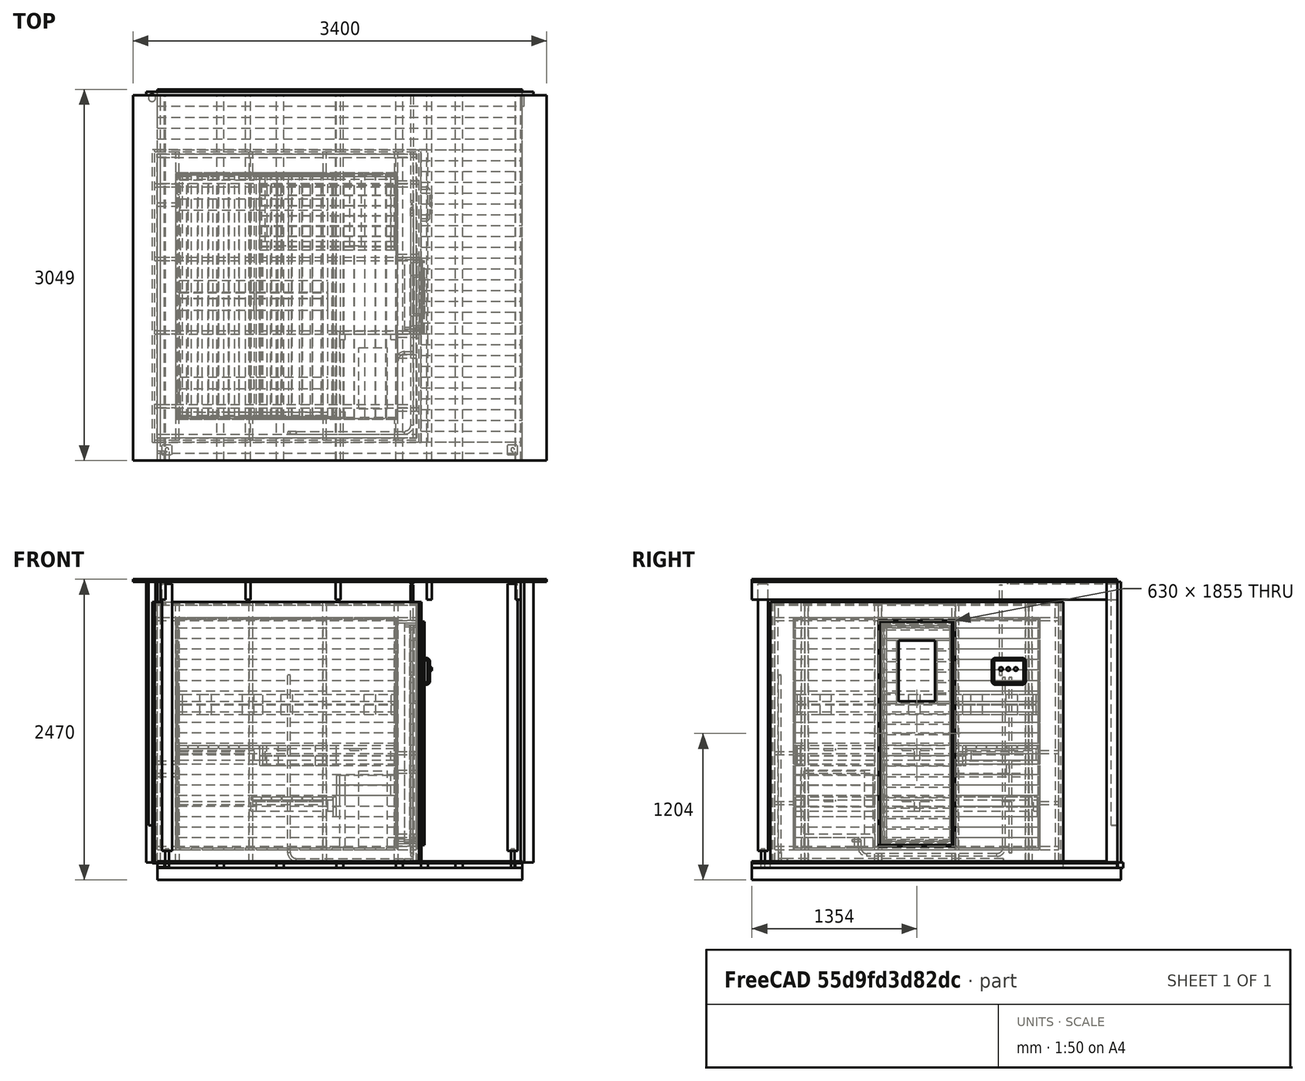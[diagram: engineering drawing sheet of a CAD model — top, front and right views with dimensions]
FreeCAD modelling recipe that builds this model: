
FCSTD DOCUMENT  (FreeCAD 0.18R16146 (Git))
Label: sauna v3
License: All rights reserved
LicenseURL: http://en.wikipedia.org/wiki/All_rights_reserved
objects: Part::Box×437, Part::Compound×38, Part::Cylinder×15, Part::Chamfer×7, Part::Torus×5, Part::Cut×5, Part::MultiFuse×4, App::DocumentObjectGroup×2, Part::Mirroring×2
note: 513 computed .brp shape members not serialized (recipe doc carries the construction recipe); baked Part::Feature solids carry a one-line shape summary decoded from their .brp

FEATURE [Part::Box] Box  label="Concrete base"
  AttacherType = Attacher::AttachEngine3D
  Height = 100
  Length = 3000
  Width = 3030
FEATURE [Part::Box] Box001  label="Wall"
  AttacherType = Attacher::AttachEngine3D
  Height = 2304
  Length = 3180
  Placement = pos=(-90,3003,144) rot=(0,0,1;0rad)
  Width = 27
FEATURE [Part::Box] Box001001  label="Wall001"
  AttacherType = Attacher::AttachEngine3D
  Height = 2304
  Length = 27
  Placement = pos=(0,2913,144) rot=(0,0,1;0rad)
  Width = 90
FEATURE [Part::Box] Box001001001  label="Wall002"
  AttacherType = Attacher::AttachEngine3D
  Height = 2304
  Length = 27
  Placement = pos=(2986,2913,144) rot=(0,0,1;0rad)
  Width = 90
FEATURE [Part::Box] Box001001002  label="Roof beam"
  AttacherType = Attacher::AttachEngine3D
  Height = 144
  Length = 3000
  Placement = pos=(69,0,2304) rot=(0,0,1;1.5708rad)
  Width = 42
FEATURE [Part::Cylinder] Cylinder  label="Pole base"
  Angle = 360
  AttacherType = Attacher::AttachEngine3D
  Height = 155
  Placement = pos=(80,90,100) rot=(0,0,1;0rad)
  Radius = 15
FEATURE [Part::Box] Box001001003  label="Pole"
  AttacherType = Attacher::AttachEngine3D
  Height = 2193
  Length = 82
  Placement = pos=(39,49,240) rot=(0,0,1;0rad)
  Width = 82
FEATURE [Part::Box] Box001001004  label="Pole support"
  AttacherType = Attacher::AttachEngine3D
  Height = 5
  Length = 100
  Placement = pos=(0,0,100) rot=(0,0,1;0rad)
  Width = 80
FEATURE [Part::Box] Box001001005  label="Roof"
  AttacherType = Attacher::AttachEngine3D
  Height = 22
  Length = 3400
  Placement = pos=(-200,0,2448) rot=(0,0,1;0rad)
  Width = 3000
FEATURE [Part::Cylinder] Cylinder001  label="Rainpipe"
  Angle = 360
  AttacherType = Attacher::AttachEngine3D
  Height = 2000
  Placement = pos=(-43,2980,448) rot=(0,0,1;0rad)
  Radius = 30
FEATURE [Part::Box] Box001001002001  label="Roof beam001"
  AttacherType = Attacher::AttachEngine3D
  Height = 144
  Length = 3000
  Placement = pos=(766,0,2304) rot=(0,0,1;1.5708rad)
  Width = 42
FEATURE [Part::Box] Box001001002001001  label="Roof beam002"
  AttacherType = Attacher::AttachEngine3D
  Height = 144
  Length = 3000
  Placement = pos=(1508,0,2304) rot=(0,0,1;1.5708rad)
  Width = 42
FEATURE [Part::Box] Box001001002001001001  label="Roof beam003"
  AttacherType = Attacher::AttachEngine3D
  Height = 144
  Length = 3000
  Placement = pos=(2255,0,2304) rot=(0,0,1;1.5708rad)
  Width = 42
FEATURE [Part::Box] Box001001002001001001001  label="Roof beam004"
  AttacherType = Attacher::AttachEngine3D
  Height = 144
  Length = 3000
  Placement = pos=(2986,0,2304) rot=(0,0,1;1.5708rad)
  Width = 42
FEATURE [Part::Cylinder] Cylinder002  label="Pole support001"
  Angle = 360
  AttacherType = Attacher::AttachEngine3D
  Height = 155
  Placement = pos=(2920,90,100) rot=(0,0,1;0rad)
  Radius = 15
FEATURE [Part::Box] Box001001003001  label="Pole001"
  AttacherType = Attacher::AttachEngine3D
  Height = 2193
  Length = 82
  Placement = pos=(2879,49,240) rot=(0,0,1;0rad)
  Width = 82
FEATURE [Part::Box] Box001001002001001001002  label="Wall base"
  AttacherType = Attacher::AttachEngine3D
  Height = 44
  Length = 3000
  Placement = pos=(0,3005,100) rot=(0,0,1;0rad)
  Width = 44
FEATURE [App::DocumentObjectGroup] Group  label="Available volume"
  Group = -> [Box,Box001,Box001001,Box001001001,Box001001002,Cylinder,Box001001003,Box001001004,Cylinder001,Box001001005,Box001001002001,Box001001002001001,Box001001002001001001,Box001001002001001001001,Cylinder002,Box001001003001,Box001001002001001001002]
FEATURE [Part::Box] Box001001002001001001003  label="B007"
  AttacherType = Attacher::AttachEngine3D
  Height = 100
  Length = 2075
  Placement = pos=(27.5,189,2158) rot=(0,0,1;0rad)
  Width = 27.5
FEATURE [Part::Box] Box001001002001001001003001  label="B008"
  AttacherType = Attacher::AttachEngine3D
  Height = 100
  Length = 2075
  Placement = pos=(27.5,434,2158) rot=(0,0,1;0rad)
  Width = 27.5
FEATURE [Part::Box] Box001001002001001001003002  label="A003"
  AttacherType = Attacher::AttachEngine3D
  Height = 100
  Length = 27.5
  Placement = pos=(0,189,2158) rot=(0,0,1;0rad)
  Width = 2330
FEATURE [Part::Box] Box001001002001001001003002001  label="A004"
  AttacherType = Attacher::AttachEngine3D
  Height = 100
  Length = 27.5
  Placement = pos=(2102.5,189,2158) rot=(0,0,1;0rad)
  Width = 2330
FEATURE [Part::Box] Box001001002001001001003002002  label="B009"
  AttacherType = Attacher::AttachEngine3D
  Height = 100
  Length = 2075
  Placement = pos=(27.5,1039,2158) rot=(0,0,1;0rad)
  Width = 27.5
FEATURE [Part::Box] Box001001002001001001003002003  label="B010"
  AttacherType = Attacher::AttachEngine3D
  Height = 100
  Length = 2075
  Placement = pos=(27.5,1644,2158) rot=(0,0,1;0rad)
  Width = 27.5
FEATURE [Part::Box] Box001001002001001001003002004  label="B011"
  AttacherType = Attacher::AttachEngine3D
  Height = 100
  Length = 2075
  Placement = pos=(27.5,2249,2158) rot=(0,0,1;0rad)
  Width = 27.5
FEATURE [Part::Box] Box001001002001001001003002005  label="B012"
  AttacherType = Attacher::AttachEngine3D
  Height = 100
  Length = 2075
  Placement = pos=(27.5,2491.5,2158) rot=(0,0,1;0rad)
  Width = 27.5
FEATURE [Part::Box] Box001001002001001001003002005003021  label="top OSB plate"
  AttacherType = Attacher::AttachEngine3D
  Height = 12
  Length = 2130
  Placement = pos=(0,189,2258) rot=(0,0,1;0rad)
  Width = 2330
FEATURE [Part::Box] Box001001002001001001003002005003022  label="I001"
  AttacherType = Attacher::AttachEngine3D
  Height = 26.5
  Length = 153
  Placement = pos=(0,189,250) rot=(0,0,1;0rad)
  Width = 2330
FEATURE [Part::Box] Box001001002001001001003002005003022001  label="I004"
  AttacherType = Attacher::AttachEngine3D
  Height = 26.5
  Length = 153
  Placement = pos=(1977,189,2131.5) rot=(0,0,1;0rad)
  Width = 2330
FEATURE [Part::Box] Box001001002001001001003002005003022001001  label="I003"
  AttacherType = Attacher::AttachEngine3D
  Height = 26.5
  Length = 153
  Placement = pos=(1977,189,250) rot=(0,0,1;0rad)
  Width = 2330
FEATURE [Part::Box] Box001001002001001001003002005003022001002  label="I002"
  AttacherType = Attacher::AttachEngine3D
  Height = 26.5
  Length = 153
  Placement = pos=(0,189,2131.5) rot=(0,0,1;0rad)
  Width = 2330
FEATURE [Part::Box] Box001001002001001001003002005003022001003  label="G001"
  AttacherType = Attacher::AttachEngine3D
  Height = 1855
  Length = 153
  Placement = pos=(0,189,276.5) rot=(0,0,1;0rad)
  Width = 26.5
FEATURE [Part::Box] Box001001002001001001003002005003022001003001  label="G002"
  AttacherType = Attacher::AttachEngine3D
  Height = 1855
  Length = 153
  Placement = pos=(0,436,276.5) rot=(0,0,1;0rad)
  Width = 26.5
FEATURE [Part::Box] Box001001002001001001003002005003022001003002  label="G003"
  AttacherType = Attacher::AttachEngine3D
  Height = 1855
  Length = 153
  Placement = pos=(0,1041,276.5) rot=(0,0,1;0rad)
  Width = 26.5
FEATURE [Part::Box] Box001001002001001001003002005003022001003003  label="G004"
  AttacherType = Attacher::AttachEngine3D
  Height = 1855
  Length = 153
  Placement = pos=(0,1646,276.5) rot=(0,0,1;0rad)
  Width = 26.5
FEATURE [Part::Box] Box001001002001001001003002005003022001003004  label="G005"
  AttacherType = Attacher::AttachEngine3D
  Height = 1855
  Length = 153
  Placement = pos=(0,2249,276.5) rot=(0,0,1;0rad)
  Width = 26.5
FEATURE [Part::Box] Box001001002001001001003002005003022001003004001  label="G006"
  AttacherType = Attacher::AttachEngine3D
  Height = 1855
  Length = 153
  Placement = pos=(0,2492.5,276.5) rot=(0,0,1;0rad)
  Width = 26.5
FEATURE [Part::Box] Box001001002001001001003002005003022001003004002001  label="F002"
  AttacherType = Attacher::AttachEngine3D
  Height = 26.5
  Length = 1824
  Placement = pos=(153,189,2131.5) rot=(0,0,1;0rad)
  Width = 153
FEATURE [Part::Box] Box001001002001001001003002005003022001003004002001001  label="F003"
  AttacherType = Attacher::AttachEngine3D
  Height = 26.5
  Length = 1824
  Placement = pos=(153,2366,2131.5) rot=(0,0,1;0rad)
  Width = 153
FEATURE [Part::Box] Box001001002001001001003002005003022001003004002001002  label="F004"
  AttacherType = Attacher::AttachEngine3D
  Height = 26.5
  Length = 1824
  Placement = pos=(153,2366,250) rot=(0,0,1;0rad)
  Width = 153
FEATURE [Part::Box] Box001001002001001001003002005003022001003001001  label="G007"
  AttacherType = Attacher::AttachEngine3D
  Height = 1855
  Length = 26.5
  Placement = pos=(153,2366,276.5) rot=(0,0,1;0rad)
  Width = 153
FEATURE [Part::Box] Box001001002001001001003002005003022001003001001001  label="G008"
  AttacherType = Attacher::AttachEngine3D
  Height = 1855
  Length = 26.5
  Placement = pos=(757.5,2366,276.5) rot=(0,0,1;0rad)
  Width = 153
FEATURE [Part::Box] Box001001002001001001003002005003022001003001001002  label="G009"
  AttacherType = Attacher::AttachEngine3D
  Height = 1855
  Length = 26.5
  Placement = pos=(1362,2366,276.5) rot=(0,0,1;0rad)
  Width = 153
FEATURE [Part::Box] Box001001002001001001003002005003022001003001001002001  label="G010"
  AttacherType = Attacher::AttachEngine3D
  Height = 1855
  Length = 26.5
  Placement = pos=(1950.5,2366,276.5) rot=(0,0,1;0rad)
  Width = 153
FEATURE [Part::Box] Box001001002001001001003002005003022001003004002001003  label="M001"
  AttacherType = Attacher::AttachEngine3D
  Height = 26.5
  Length = 578
  Placement = pos=(179.5,189,1029) rot=(0,0,1;0rad)
  Width = 153
FEATURE [Part::Box] Box001001002001001001003002005003022001003004002001003001  label="M002"
  AttacherType = Attacher::AttachEngine3D
  Height = 26.5
  Length = 578
  Placement = pos=(784,189,619) rot=(0,0,1;0rad)
  Width = 153
FEATURE [Part::Box] Box001001002001001001003002005003022001003001001002002  label="G011"
  AttacherType = Attacher::AttachEngine3D
  Height = 1855
  Length = 26.5
  Placement = pos=(153,189,276.5) rot=(0,0,1;0rad)
  Width = 153
FEATURE [Part::Box] Box001001002001001001003002005003022001003004002001003002  label="M003"
  AttacherType = Attacher::AttachEngine3D
  Height = 26.5
  Length = 578
  Placement = pos=(179.5,2366,1039) rot=(0,0,1;0rad)
  Width = 153
FEATURE [Part::Box] Box001001002001001001003002005003022001003004002001003001001  label="M004"
  AttacherType = Attacher::AttachEngine3D
  Height = 26.5
  Length = 578
  Placement = pos=(784,2366,619) rot=(0,0,1;0rad)
  Width = 153
FEATURE [Part::Box] Box001001002001001001003002005003022001003001001001001  label="G012"
  AttacherType = Attacher::AttachEngine3D
  Height = 1855
  Length = 26.5
  Placement = pos=(757.5,189,276.5) rot=(0,0,1;0rad)
  Width = 153
FEATURE [Part::Box] Box001001002001001001003002005003022001003001001002003  label="G013"
  AttacherType = Attacher::AttachEngine3D
  Height = 1855
  Length = 26.5
  Placement = pos=(1362,189,276.5) rot=(0,0,1;0rad)
  Width = 153
FEATURE [Part::Box] Box001001002001001001003002005003022001003001001002001001  label="G014"
  AttacherType = Attacher::AttachEngine3D
  Height = 1855
  Length = 26.5
  Placement = pos=(1950.5,189,276.5) rot=(0,0,1;0rad)
  Width = 153
FEATURE [Part::Box] Box001001002001001001003002005003022001003004002  label="F001"
  AttacherType = Attacher::AttachEngine3D
  Height = 26.5
  Length = 1824
  Placement = pos=(153,189,250) rot=(0,0,1;0rad)
  Width = 153
FEATURE [Part::Box] Box001001002001001001003002005003022001003004002001003001002  label="G015"
  AttacherType = Attacher::AttachEngine3D
  Height = 1855
  Length = 153
  Placement = pos=(1977,189,276.5) rot=(0,0,1;0rad)
  Width = 26.5
FEATURE [Part::Box] Box001001002001001001003002005003022001003001001002001002  label="G016"
  AttacherType = Attacher::AttachEngine3D
  Height = 1855
  Length = 153
  Placement = pos=(1977,408,276.5) rot=(0,0,1;0rad)
  Width = 26.5
FEATURE [Part::Box] Box001001002001001001003002005003022001003002001  label="G017"
  AttacherType = Attacher::AttachEngine3D
  Height = 1855
  Length = 153
  Placement = pos=(1977,1012.5,276.5) rot=(0,0,1;0rad)
  Width = 26.5
FEATURE [Part::Box] Box001001002001001001003002005003022001003003001  label="G018"
  AttacherType = Attacher::AttachEngine3D
  Height = 1855
  Length = 153
  Placement = pos=(1977,1669,276.5) rot=(0,0,1;0rad)
  Width = 26.5
FEATURE [Part::Box] Box001001002001001001003002005003022001003004002001003001003  label="G019"
  AttacherType = Attacher::AttachEngine3D
  Height = 1855
  Length = 153
  Placement = pos=(1977,2273.5,276.5) rot=(0,0,1;0rad)
  Width = 26.5
FEATURE [Part::Box] Box001001002001001001003002005003022001003004001001  label="G020"
  AttacherType = Attacher::AttachEngine3D
  Height = 1855
  Length = 153
  Placement = pos=(1977,2492.5,276.5) rot=(0,0,1;0rad)
  Width = 26.5
FEATURE [Part::Box] Box001001002001001001003002005003022001003004002001003001004  label="M005"
  AttacherType = Attacher::AttachEngine3D
  Height = 26.5
  Length = 153
  Placement = pos=(1977,434.5,877) rot=(0,0,1;0rad)
  Width = 578
FEATURE [Part::Box] Box001001002001001001003002005003022001003004002001003001004001  label="M006"
  AttacherType = Attacher::AttachEngine3D
  Height = 26.5
  Length = 153
  Placement = pos=(1977,1695.5,1029) rot=(0,0,1;0rad)
  Width = 578
FEATURE [Part::Box] Box001001002001001001003002005003022001003004002001003001004002  label="Y001"
  AttacherType = Attacher::AttachEngine3D
  Height = 95
  Length = 15
  Placement = pos=(168,357,985) rot=(0,0,1;0rad)
  Width = 1994
FEATURE [Part::Box] Box001001002001001001003002005003022001003004002001003001004002001  label="Y002"
  AttacherType = Attacher::AttachEngine3D
  Height = 80
  Length = 25
  Placement = pos=(843,362,941) rot=(0,0,1;0rad)
  Width = 1371
FEATURE [Part::Box] Box001001002001001001003002005003022001003004002001003001004002002  label="Z001"
  AttacherType = Attacher::AttachEngine3D
  Height = 95
  Length = 616
  Placement = pos=(183,357,985) rot=(0,0,1;0rad)
  Width = 44
FEATURE [Part::Box] Box001001002001001001003002005003022001003004002001003001004002002001  label="Z002"
  AttacherType = Attacher::AttachEngine3D
  Height = 95
  Length = 616
  Placement = pos=(183,2307,985) rot=(0,0,1;0rad)
  Width = 44
FEATURE [Part::Box] Box001001002001001001003002005003022001003004002001003001004002002001001  label="Z003"
  AttacherType = Attacher::AttachEngine3D
  Height = 95
  Length = 588
  Placement = pos=(814,2313,565) rot=(0,0,1;0rad)
  Width = 44
FEATURE [Part::Box] Box001001002001001001003002005003022001003004002001003001004002001001  label="J021"
  AttacherType = Attacher::AttachEngine3D
  Height = 80
  Length = 25
  Placement = pos=(1446,362,605) rot=(0,0,1;0rad)
  Width = 1984
FEATURE [Part::Box] Box001001002001001001003002005003022001003004002001003001004002002001002  label="Y004"
  AttacherType = Attacher::AttachEngine3D
  Height = 95
  Length = 44
  Placement = pos=(770,357,565) rot=(0,0,1;0rad)
  Width = 1994
FEATURE [Part::Box] Box001001002001001001003002005003022001003004002001003001004002002001003  label="Z004"
  AttacherType = Attacher::AttachEngine3D
  Height = 95
  Length = 588
  Placement = pos=(814,357,565) rot=(0,0,1;0rad)
  Width = 44
FEATURE [Part::Box] Box001001002001001001003002005003022001003004002001003001004002002001004  label="H001"
  AttacherType = Attacher::AttachEngine3D
  Height = 95
  Length = 1119
  Placement = pos=(843,2336,985) rot=(0,0,1;0rad)
  Width = 15
FEATURE [Part::Box] Box001001002001001001003002005003022001003004002001003001004002002001004001  label="H002"
  AttacherType = Attacher::AttachEngine3D
  Height = 80
  Length = 603
  Placement = pos=(868,372,1025) rot=(0,0,1;0rad)
  Width = 25
FEATURE [Part::Box] Box001001002001001001003002005003022001003004002001003001004002002001004002  label="AI001"
  AttacherType = Attacher::AttachEngine3D
  Height = 95
  Length = 44
  Placement = pos=(843,1802,985) rot=(0,0,1;0rad)
  Width = 534
FEATURE [Part::Box] Box001001002001001001003002005003022001003004002001003001004002002001004002001  label="AI002"
  AttacherType = Attacher::AttachEngine3D
  Height = 95
  Length = 44
  Placement = pos=(1918,1802,985) rot=(0,0,1;0rad)
  Width = 534
FEATURE [Part::Box] Box001001002001001001003002005003022001003004002001003001004002002001004002002  label="Z007"
  AttacherType = Attacher::AttachEngine3D
  Height = 95
  Length = 616
  Placement = pos=(183,1335,985) rot=(0,0,1;0rad)
  Width = 44
FEATURE [Part::Box] Box001001002001001001003002005003022001003004002001003001004002002001003001  label="Z008"
  AttacherType = Attacher::AttachEngine3D
  Height = 95
  Length = 588
  Placement = pos=(814,1335,565) rot=(0,0,1;0rad)
  Width = 44
FEATURE [Part::Box] Box001001002001001001003002005003022001003004002001003001004002002001004002003  label="J001"
  AttacherType = Attacher::AttachEngine3D
  Height = 25
  Length = 80
  Placement = pos=(171,362,1080) rot=(0,0,1;0rad)
  Width = 1984
FEATURE [Part::Box] Box001001002001001001003002005003022001003004002001003001004002002001004002003001  label="J002"
  AttacherType = Attacher::AttachEngine3D
  Height = 25
  Length = 80
  Placement = pos=(255,362,1080) rot=(0,0,1;0rad)
  Width = 1984
FEATURE [Part::Box] Box001001002001001001003002005003022001003004002001003001004002002001004002003002  label="J003"
  AttacherType = Attacher::AttachEngine3D
  Height = 25
  Length = 80
  Placement = pos=(339,362,1080) rot=(0,0,1;0rad)
  Width = 1984
FEATURE [Part::Box] Box001001002001001001003002005003022001003004002001003001004002002001004002003003  label="J004"
  AttacherType = Attacher::AttachEngine3D
  Height = 25
  Length = 80
  Placement = pos=(423,362,1080) rot=(0,0,1;0rad)
  Width = 1984
FEATURE [Part::Box] Box001001002001001001003002005003022001003004002001003001004002002001004002003004  label="J005"
  AttacherType = Attacher::AttachEngine3D
  Height = 25
  Length = 80
  Placement = pos=(507,362,1080) rot=(0,0,1;0rad)
  Width = 1984
FEATURE [Part::Box] Box001001002001001001003002005003022001003004002001003001004002002001004002003005  label="J006"
  AttacherType = Attacher::AttachEngine3D
  Height = 25
  Length = 80
  Placement = pos=(591,362,1080) rot=(0,0,1;0rad)
  Width = 1984
FEATURE [Part::Box] Box001001002001001001003002005003022001003004002001003001004002002001004002003005001  label="J007"
  AttacherType = Attacher::AttachEngine3D
  Height = 25
  Length = 80
  Placement = pos=(1278,362,660) rot=(0,0,1;0rad)
  Width = 1984
FEATURE [Part::Box] Box001001002001001001003002005003022001003004002001003001004002002001004002003005002  label="J008"
  AttacherType = Attacher::AttachEngine3D
  Height = 25
  Length = 80
  Placement = pos=(858,362,660) rot=(0,0,1;0rad)
  Width = 1984
FEATURE [Part::Box] Box001001002001001001003002005003022001003004002001003001004002002001004002003001001  label="J009"
  AttacherType = Attacher::AttachEngine3D
  Height = 25
  Length = 80
  Placement = pos=(942,362,660) rot=(0,0,1;0rad)
  Width = 1984
FEATURE [Part::Box] Box001001002001001001003002005003022001003004002001003001004002002001004002003002001  label="J010"
  AttacherType = Attacher::AttachEngine3D
  Height = 25
  Length = 80
  Placement = pos=(1026,362,660) rot=(0,0,1;0rad)
  Width = 1984
FEATURE [Part::Box] Box001001002001001001003002005003022001003004002001003001004002002001004002003003001  label="J011"
  AttacherType = Attacher::AttachEngine3D
  Height = 25
  Length = 80
  Placement = pos=(1110,362,660) rot=(0,0,1;0rad)
  Width = 1984
FEATURE [Part::Box] Box001001002001001001003002005003022001003004002001003001004002002001004002003004001  label="J012"
  AttacherType = Attacher::AttachEngine3D
  Height = 25
  Length = 80
  Placement = pos=(1194,362,660) rot=(0,0,1;0rad)
  Width = 1984
FEATURE [Part::Box] Box001001002001001001003002005003022001003004002001003001004002002001004002003005003  label="C001"
  AttacherType = Attacher::AttachEngine3D
  Height = 25
  Length = 1114
  Placement = pos=(843,1846,1080) rot=(0,0,1;0rad)
  Width = 80
FEATURE [Part::Box] Box001001002001001001003002005003022001003004002001003001004002002001004002003005003001  label="C002"
  AttacherType = Attacher::AttachEngine3D
  Height = 25
  Length = 1114
  Placement = pos=(843,1930,1080) rot=(0,0,1;0rad)
  Width = 80
FEATURE [Part::Box] Box001001002001001001003002005003022001003004002001003001004002002001004002003005003002  label="C003"
  AttacherType = Attacher::AttachEngine3D
  Height = 25
  Length = 1114
  Placement = pos=(843,2014,1080) rot=(0,0,1;0rad)
  Width = 80
FEATURE [Part::Box] Box001001002001001001003002005003022001003004002001003001004002002001004002003005003003  label="C004"
  AttacherType = Attacher::AttachEngine3D
  Height = 25
  Length = 1114
  Placement = pos=(843,2098,1080) rot=(0,0,1;0rad)
  Width = 80
FEATURE [Part::Box] Box001001002001001001003002005003022001003004002001003001004002002001004002003005003004  label="C005"
  AttacherType = Attacher::AttachEngine3D
  Height = 25
  Length = 1114
  Placement = pos=(843,2182,1080) rot=(0,0,1;0rad)
  Width = 80
FEATURE [Part::Box] Box001001002001001001003002005003022001003004002001003001004002002001004002003005003005  label="C006"
  AttacherType = Attacher::AttachEngine3D
  Height = 25
  Length = 1114
  Placement = pos=(843,2266,1080) rot=(0,0,1;0rad)
  Width = 80
FEATURE [Part::Box] Box001001002001001001003002005003022001003004002001003001004002002001004002003005003005001  label="D001"
  AttacherType = Attacher::AttachEngine3D
  Height = 15
  Length = 610
  Placement = pos=(186,2057,1065) rot=(0,0,1;0rad)
  Width = 95
FEATURE [Part::Box] Box001001002001001001003002005003022001003004002001003001004002002001004002003005003005001001  label="D002"
  AttacherType = Attacher::AttachEngine3D
  Height = 15
  Length = 610
  Placement = pos=(186,592,1065) rot=(0,0,1;0rad)
  Width = 95
FEATURE [Part::Box] Box001001002001001001003002005003022001003004002001003001004002002001004002003005003005001002  label="D003"
  AttacherType = Attacher::AttachEngine3D
  Height = 15
  Length = 586
  Placement = pos=(815,2057,645) rot=(0,0,1;0rad)
  Width = 95
FEATURE [Part::Box] Box001001002001001001003002005003022001003004002001003001004002002001004002003005003005001001001  label="D004"
  AttacherType = Attacher::AttachEngine3D
  Height = 15
  Length = 586
  Placement = pos=(815,592,645) rot=(0,0,1;0rad)
  Width = 95
FEATURE [Part::Box] Box001001002001001001003002005003022001003004002001003001004002002001004002003005003005001001002  label="D005"
  AttacherType = Attacher::AttachEngine3D
  Height = 15
  Length = 95
  Placement = pos=(984,1767,1065) rot=(0,0,1;0rad)
  Width = 568
FEATURE [Part::Box] Box001001002001001001003002005003022001003004002001003001004002002001004002003005003005001001002001  label="D006"
  AttacherType = Attacher::AttachEngine3D
  Height = 15
  Length = 95
  Placement = pos=(1584,1767,1065) rot=(0,0,1;0rad)
  Width = 568
FEATURE [Part::Box] Box001001002001001001003002005003022001003004002001003001004002002001004002003005003005001001002002  label="M007"
  AttacherType = Attacher::AttachEngine3D
  Height = 26.5
  Length = 578
  Placement = pos=(179.5,189,619) rot=(0,0,1;0rad)
  Width = 153
FEATURE [Part::Box] Box001001002001001001003002005003022001003004002001003001001001  label="M008"
  AttacherType = Attacher::AttachEngine3D
  Height = 26.5
  Length = 578
  Placement = pos=(179.5,2366,619) rot=(0,0,1;0rad)
  Width = 153
FEATURE [Part::Box] Box001001002001001001003002005003022001003004002001003001004002002001004002003005003005001001002003  label="J013"
  AttacherType = Attacher::AttachEngine3D
  Height = 25
  Length = 80
  Placement = pos=(675,362,1080) rot=(0,0,1;0rad)
  Width = 1984
FEATURE [Part::Box] Box001001002001001001003002005003022001003004002001003001004002002001004002003005001001  label="J014"
  AttacherType = Attacher::AttachEngine3D
  Height = 25
  Length = 80
  Placement = pos=(1362,362,660) rot=(0,0,1;0rad)
  Width = 1984
FEATURE [Part::Box] Box001001002001001001003002005003022001003004002001003001004002002001004002003005003005001001002004  label="Heather"
  AttacherType = Attacher::AttachEngine3D
  Height = 630
  Length = 235
  Placement = pos=(1657,427,265) rot=(0,0,1;0rad)
  Width = 500
FEATURE [Part::Box] Box001001002001001001003002005003022001003004002001003001004002002001004002003005001001001001  label="AA001"
  AttacherType = Attacher::AttachEngine3D
  Height = 80
  Length = 25
  Placement = pos=(1475,357,698) rot=(0,0,1;0rad)
  Width = 707
FEATURE [Part::Box] Box001001002001001001003002005003022001003004002001003001004002002001004002003005001001001001001  label="AA002"
  AttacherType = Attacher::AttachEngine3D
  Height = 80
  Length = 25
  Placement = pos=(1475,357,782) rot=(0,0,1;0rad)
  Width = 707
FEATURE [Part::Box] Box001001002001001001003002005003022001003004002001003001004002002001004002003005001001001001001001  label="AB001"
  AttacherType = Attacher::AttachEngine3D
  Height = 80
  Length = 472
  Placement = pos=(1500,1039,782) rot=(0,0,1;0rad)
  Width = 25
FEATURE [Part::Box] Box001001002001001001003002005003022001003004002001003001004002002001004002003005001001001001001001001  label="AB002"
  AttacherType = Attacher::AttachEngine3D
  Height = 80
  Length = 472
  Placement = pos=(1500,1039,698) rot=(0,0,1;0rad)
  Width = 25
FEATURE [Part::Box] Box001001002001001001003002005003022001003004002001003001004002002001004002003005001001001001001001002  label="AC001"
  AttacherType = Attacher::AttachEngine3D
  Height = 592
  Length = 44
  Placement = pos=(1500,995,270) rot=(0,0,1;0rad)
  Width = 44
FEATURE [Part::Box] Box001001002001001001003002005003022001003004002001003001004002002001004002003005001001001001001001002001  label="AD001"
  AttacherType = Attacher::AttachEngine3D
  Height = 164
  Length = 44
  Placement = pos=(1500,357,698) rot=(0,0,1;0rad)
  Width = 44
FEATURE [Part::Box] Box001001002001001001003002005003022001003004002001003001004002002001004002003005001001001001001001002001001  label="AD002"
  AttacherType = Attacher::AttachEngine3D
  Height = 164
  Length = 44
  Placement = pos=(1918,995,698) rot=(0,0,1;0rad)
  Width = 44
FEATURE [Part::Box] Box001001002001001001003002005003022001003004002001003001004002002001004002003005003005001001002005  label="D007"
  AttacherType = Attacher::AttachEngine3D
  Height = 15
  Length = 610
  Placement = pos=(186,1235,1065) rot=(0,0,1;0rad)
  Width = 95
FEATURE [Part::Box] Box001001002001001001003002005003022001003004002001003001004002002001004002003005003005001001002006  label="D008"
  AttacherType = Attacher::AttachEngine3D
  Height = 15
  Length = 610
  Placement = pos=(186,1385,1065) rot=(0,0,1;0rad)
  Width = 95
FEATURE [Part::Box] Box001001002001001001003002005003022001003004002001003001004002002001004002003005003005001002001  label="D009"
  AttacherType = Attacher::AttachEngine3D
  Height = 15
  Length = 586
  Placement = pos=(815,1385,645) rot=(0,0,1;0rad)
  Width = 95
FEATURE [Part::Box] Box001001002001001001003002005003022001003004002001003001004002002001004002003005003005001002002  label="D010"
  AttacherType = Attacher::AttachEngine3D
  Height = 15
  Length = 586
  Placement = pos=(815,1235,645) rot=(0,0,1;0rad)
  Width = 95
FEATURE [Part::Box] Box001001002001001001003002005003022001003004002001003001004002002001004002003005001001001001001001002001002  label="J015"
  AttacherType = Attacher::AttachEngine3D
  Height = 80
  Length = 25
  Placement = pos=(1922,1733,1361) rot=(0,0,1;0rad)
  Width = 578
FEATURE [Part::Box] Box001001002001001001003002005003022001003004002001003001004002002001004002003005001001001001001001002001002001  label="J016"
  AttacherType = Attacher::AttachEngine3D
  Height = 80
  Length = 25
  Placement = pos=(183,372,1445) rot=(0,0,1;0rad)
  Width = 1964
FEATURE [Part::Box] Box001001002001001001003002005003022001003004002001003001004002002001004002003005001001001001001001002001002001001  label="AE001"
  AttacherType = Attacher::AttachEngine3D
  Height = 164
  Length = 15
  Placement = pos=(168,559,1361) rot=(0,0,1;0rad)
  Width = 95
FEATURE [Part::Box] Box001001002001001001003002005003022001003004002001003001004002002001004002003005001001001001001001002001002001001001  label="AE002"
  AttacherType = Attacher::AttachEngine3D
  Height = 164
  Length = 15
  Placement = pos=(168,1289,1361) rot=(0,0,1;0rad)
  Width = 95
FEATURE [Part::Box] Box001001002001001001003002005003022001003004002001003001004002002001004002003005001001001001001001002001002001001002  label="AE003"
  AttacherType = Attacher::AttachEngine3D
  Height = 164
  Length = 15
  Placement = pos=(168,2089,1361) rot=(0,0,1;0rad)
  Width = 95
FEATURE [Part::Box] Box001001002001001001003002005003022001003004002001003001004002002001004002003005001001001001001001002001002001001003  label="AF001"
  AttacherType = Attacher::AttachEngine3D
  Height = 80
  Length = 660
  Placement = pos=(207,372,1361) rot=(0,0,1;0rad)
  Width = 25
FEATURE [Part::Box] Box001001002001001001003002005003022001003004002001003001004002002001004002003005001001001001001001002001002001001004  label="M009"
  AttacherType = Attacher::AttachEngine3D
  Height = 26.5
  Length = 153
  Placement = pos=(1977,434.5,352) rot=(0,0,1;0rad)
  Width = 578
FEATURE [Part::Box] Box001001002001001001003002005003022001003001001002001002001  label="AH002"
  AttacherType = Attacher::AttachEngine3D
  Height = 75
  Length = 153
  Placement = pos=(1977,844,277) rot=(0,0,1;0rad)
  Width = 26.5
FEATURE [Part::Box] Box001001002001001001003002005003022001003004002001003001004002002001004002003005001001001001001001002001002001001003001  label="AF002"
  AttacherType = Attacher::AttachEngine3D
  Height = 80
  Length = 1739
  Placement = pos=(208,2311,1445) rot=(0,0,1;0rad)
  Width = 25
FEATURE [Part::Box] Box001001002001001001003002005003022001003004002001003001004002002001004002003005001001001001001001002001002001001003002  label="AE004"
  AttacherType = Attacher::AttachEngine3D
  Height = 164
  Length = 95
  Placement = pos=(350,2336,1361) rot=(0,0,1;0rad)
  Width = 15
FEATURE [Part::Box] Box001001002001001001003002005003022001003004002001003001004002002001004002003005001001001001001001002001002001001003002001  label="AE005"
  AttacherType = Attacher::AttachEngine3D
  Height = 164
  Length = 95
  Placement = pos=(1016,2336,1361) rot=(0,0,1;0rad)
  Width = 15
FEATURE [Part::Box] Box001001002001001001003002005003022001003004002001003001004002002001004002003005001001001001001001002001002001001003002002  label="AE006"
  AttacherType = Attacher::AttachEngine3D
  Height = 164
  Length = 95
  Placement = pos=(1700,2336,1361) rot=(0,0,1;0rad)
  Width = 15
FEATURE [Part::Box] Box001001002001001001003002005003022001003004002001003001004002002001004002003005001001001001001001002001002001001004001  label="M010"
  AttacherType = Attacher::AttachEngine3D
  Height = 26.5
  Length = 153
  Placement = pos=(0,1671,951.5) rot=(0,0,1;0rad)
  Width = 578
FEATURE [Part::Box] Box001001002001001001003002005003022001003004002001003001004002002001004002003005001001001001001001002001002001001004001001  label="M011"
  AttacherType = Attacher::AttachEngine3D
  Height = 26.5
  Length = 153
  Placement = pos=(0,1671,850) rot=(0,0,1;0rad)
  Width = 578
FEATURE [Part::Box] Box001001002001001001003002005003022001003004002001003001004002002001004002003005001001001001001001002001002001001004001001001  label="AH001"
  AttacherType = Attacher::AttachEngine3D
  Height = 75
  Length = 153
  Placement = pos=(0,2091,876.5) rot=(0,0,1;0rad)
  Width = 26.5
FEATURE [Part::Box] Box001001002001001001003002005003022001003004002001003001004002002001004002003005001001001001001001002001002001001004001001002  label="Terrasbalk001"
  AttacherType = Attacher::AttachEngine3D
  Height = 38
  Length = 58
  Placement = pos=(0,0,100) rot=(0,0,1;0rad)
  Width = 3000
FEATURE [Part::Box] Box001001002001001001003002005003022001003004002001003001004002002001004002003005001001001001001001002001002001001004001001002001  label="Terrasbalk002"
  AttacherType = Attacher::AttachEngine3D
  Height = 38
  Length = 58
  Placement = pos=(490,0,100) rot=(0,0,1;0rad)
  Width = 3000
FEATURE [Part::Box] Box001001002001001001003002005003022001003004002001003001004002002001004002003005001001001001001001002001002001001004001001002002  label="Terrasbalk003"
  AttacherType = Attacher::AttachEngine3D
  Height = 38
  Length = 58
  Placement = pos=(980,0,100) rot=(0,0,1;0rad)
  Width = 3000
FEATURE [Part::Box] Box001001002001001001003002005003022001003004002001003001004002002001004002003005001001001001001001002001002001001004001001002002001005005  label="Terrasplank001"
  AttacherType = Attacher::AttachEngine3D
  Height = 15.5
  Length = 3000
  Placement = pos=(0,0,138) rot=(0,0,1;0rad)
  Width = 63
FEATURE [Part::Box] Box001001002001001001003002005003022001003004002001003001004002002001004002003005001001001001001001002001002001001004001001002002001005005001  label="Terrasplank002"
  AttacherType = Attacher::AttachEngine3D
  Height = 15.5
  Length = 3000
  Placement = pos=(0,63,138) rot=(0,0,1;0rad)
  Width = 89
FEATURE [Part::Box] Box001001002001001001003002005003022001003004002001003001004002002001004002003005001001001001001001002001002001001004001001002002001005005002  label="TerrasplankA001"
  AttacherType = Attacher::AttachEngine3D
  Height = 15.5
  Length = 833
  Placement = pos=(2167,152,138) rot=(0,0,1;0rad)
  Width = 89
FEATURE [Part::Box] Box001001002001001001003002005003022001003004002001003001004002002001004002003005001001001001001001002001002001001004001001002002001005005002001  label="TerrasplankA002"
  AttacherType = Attacher::AttachEngine3D
  Height = 15.5
  Length = 833
  Placement = pos=(2167,241,138) rot=(0,0,1;0rad)
  Width = 89
FEATURE [Part::Box] Box001001002001001001003002005003022001003004002001003001004002002001004002003005001001001001001001002001002001001004001001002002001005005002002  label="TerrasplankA003"
  AttacherType = Attacher::AttachEngine3D
  Height = 15.5
  Length = 833
  Placement = pos=(2167,330,138) rot=(0,0,1;0rad)
  Width = 89
FEATURE [Part::Box] Box001001002001001001003002005003022001003004002001003001004002002001004002003005001001001001001001002001002001001004001001002002001005005002003  label="TerrasplankA004"
  AttacherType = Attacher::AttachEngine3D
  Height = 15.5
  Length = 833
  Placement = pos=(2167,419,138) rot=(0,0,1;0rad)
  Width = 89
FEATURE [Part::Box] Box001001002001001001003002005003022001003004002001003001004002002001004002003005001001001001001001002001002001001004001001002002001005005002004  label="TerrasplankA005"
  AttacherType = Attacher::AttachEngine3D
  Height = 15.5
  Length = 833
  Placement = pos=(2167,508,138) rot=(0,0,1;0rad)
  Width = 89
FEATURE [Part::Box] Box001001002001001001003002005003022001003004002001003001004002002001004002003005001001001001001001002001002001001004001001002002001005005002005  label="TerrasplankA006"
  AttacherType = Attacher::AttachEngine3D
  Height = 15.5
  Length = 833
  Placement = pos=(2167,597,138) rot=(0,0,1;0rad)
  Width = 89
FEATURE [Part::Box] Box001001002001001001003002005003022001003004002001003001004002002001004002003005001001001001001001002001002001001004001001002002001005005002006  label="TerrasplankA007"
  AttacherType = Attacher::AttachEngine3D
  Height = 15.5
  Length = 833
  Placement = pos=(2167,686,138) rot=(0,0,1;0rad)
  Width = 89
FEATURE [Part::Box] Box001001002001001001003002005003022001003004002001003001004002002001004002003005001001001001001001002001002001001004001001002002001005005002007  label="TerrasplankA008"
  AttacherType = Attacher::AttachEngine3D
  Height = 15.5
  Length = 833
  Placement = pos=(2167,775,138) rot=(0,0,1;0rad)
  Width = 89
FEATURE [Part::Box] Box001001002001001001003002005003022001003004002001003001004002002001004002003005001001001001001001002001002001001004001001002002001005005002008  label="TerrasplankA009"
  AttacherType = Attacher::AttachEngine3D
  Height = 15.5
  Length = 833
  Placement = pos=(2167,864,138) rot=(0,0,1;0rad)
  Width = 89
FEATURE [Part::Box] Box001001002001001001003002005003022001003004002001003001004002002001004002003005001001001001001001002001002001001004001001002002001005005002009  label="TerrasplankA010"
  AttacherType = Attacher::AttachEngine3D
  Height = 15.5
  Length = 833
  Placement = pos=(2167,953,138) rot=(0,0,1;0rad)
  Width = 89
FEATURE [Part::Box] Box001001002001001001003002005003022001003004002001003001004002002001004002003005001001001001001001002001002001001004001001002002001005005002010  label="TerrasplankA011"
  AttacherType = Attacher::AttachEngine3D
  Height = 15.5
  Length = 833
  Placement = pos=(2167,1042,138) rot=(0,0,1;0rad)
  Width = 89
FEATURE [Part::Box] Box001001002001001001003002005003022001003004002001003001004002002001004002003005001001001001001001002001002001001004001001002002001005005002010001  label="TerrasplankA012"
  AttacherType = Attacher::AttachEngine3D
  Height = 15.5
  Length = 833
  Placement = pos=(2167,1131,138) rot=(0,0,1;0rad)
  Width = 89
FEATURE [Part::Box] Box001001002001001001003002005003022001003004002001003001004002002001004002003005001001001001001001002001002001001004001001002002001005005002010002  label="TerrasplankA013"
  AttacherType = Attacher::AttachEngine3D
  Height = 15.5
  Length = 833
  Placement = pos=(2167,1220,138) rot=(0,0,1;0rad)
  Width = 89
FEATURE [Part::Box] Box001001002001001001003002005003022001003004002001003001004002002001004002003005001001001001001001002001002001001004001001002002001005005002010003  label="TerrasplankA014"
  AttacherType = Attacher::AttachEngine3D
  Height = 15.5
  Length = 833
  Placement = pos=(2167,1309,138) rot=(0,0,1;0rad)
  Width = 89
FEATURE [Part::Box] Box001001002001001001003002005003022001003004002001003001004002002001004002003005001001001001001001002001002001001004001001002002001005005002010004  label="TerrasplankA015"
  AttacherType = Attacher::AttachEngine3D
  Height = 15.5
  Length = 833
  Placement = pos=(2167,1398,138) rot=(0,0,1;0rad)
  Width = 89
FEATURE [Part::Box] Box001001002001001001003002005003022001003004002001003001004002002001004002003005001001001001001001002001002001001004001001002002001005005002010005  label="TerrasplankA016"
  AttacherType = Attacher::AttachEngine3D
  Height = 15.5
  Length = 833
  Placement = pos=(2167,1487,138) rot=(0,0,1;0rad)
  Width = 89
FEATURE [Part::Box] Box001001002001001001003002005003022001003004002001003001004002002001004002003005001001001001001001002001002001001004001001002002001005005002010006  label="TerrasplankA017"
  AttacherType = Attacher::AttachEngine3D
  Height = 15.5
  Length = 833
  Placement = pos=(2167,1576,138) rot=(0,0,1;0rad)
  Width = 89
FEATURE [Part::Box] Box001001002001001001003002005003022001003004002001003001004002002001004002003005001001001001001001002001002001001004001001002002001005005002010007  label="TerrasplankA018"
  AttacherType = Attacher::AttachEngine3D
  Height = 15.5
  Length = 833
  Placement = pos=(2167,1665,138) rot=(0,0,1;0rad)
  Width = 89
FEATURE [Part::Box] Box001001002001001001003002005003022001003004002001003001004002002001004002003005001001001001001001002001002001001004001001002002001005005002010008  label="TerrasplankA019"
  AttacherType = Attacher::AttachEngine3D
  Height = 15.5
  Length = 833
  Placement = pos=(2167,1754,138) rot=(0,0,1;0rad)
  Width = 89
FEATURE [Part::Box] Box001001002001001001003002005003022001003004002001003001004002002001004002003005001001001001001001002001002001001004001001002002001005005002010009  label="TerrasplankA020"
  AttacherType = Attacher::AttachEngine3D
  Height = 15.5
  Length = 833
  Placement = pos=(2167,1843,138) rot=(0,0,1;0rad)
  Width = 89
FEATURE [Part::Box] Box001001002001001001003002005003022001003004002001003001004002002001004002003005001001001001001001002001002001001004001001002002001005005002010010  label="TerrasplankA021"
  AttacherType = Attacher::AttachEngine3D
  Height = 15.5
  Length = 833
  Placement = pos=(2167,1932,138) rot=(0,0,1;0rad)
  Width = 89
FEATURE [Part::Box] Box001001002001001001003002005003022001003004002001003001004002002001004002003005001001001001001001002001002001001004001001002002001005005002010011  label="TerrasplankA022"
  AttacherType = Attacher::AttachEngine3D
  Height = 15.5
  Length = 833
  Placement = pos=(2167,2021,138) rot=(0,0,1;0rad)
  Width = 89
FEATURE [Part::Box] Box001001002001001001003002005003022001003004002001003001004002002001004002003005001001001001001001002001002001001004001001002002001005005002010012  label="TerrasplankA023"
  AttacherType = Attacher::AttachEngine3D
  Height = 15.5
  Length = 833
  Placement = pos=(2167,2110,138) rot=(0,0,1;0rad)
  Width = 89
FEATURE [Part::Box] Box001001002001001001003002005003022001003004002001003001004002002001004002003005001001001001001001002001002001001004001001002002001005005002010013  label="TerrasplankA024"
  AttacherType = Attacher::AttachEngine3D
  Height = 15.5
  Length = 833
  Placement = pos=(2167,2199,138) rot=(0,0,1;0rad)
  Width = 89
FEATURE [Part::Box] Box001001002001001001003002005003022001003004002001003001004002002001004002003005001001001001001001002001002001001004001001002002001005005002010014  label="TerrasplankA025"
  AttacherType = Attacher::AttachEngine3D
  Height = 15.5
  Length = 833
  Placement = pos=(2167,2288,138) rot=(0,0,1;0rad)
  Width = 89
FEATURE [Part::Box] Box001001002001001001003002005003022001003004002001003001004002002001004002003005001001001001001001002001002001001004001001002002001005005002010015  label="TerrasplankA026"
  AttacherType = Attacher::AttachEngine3D
  Height = 15.5
  Length = 833
  Placement = pos=(2167,2377,138) rot=(0,0,1;0rad)
  Width = 89
FEATURE [Part::Box] Box001001002001001001003002005003022001003004002001003001004002002001004002003005001001001001001001002001002001001004001001002002001005005002010015001  label="TerrasplankA027"
  AttacherType = Attacher::AttachEngine3D
  Height = 15.5
  Length = 833
  Placement = pos=(2167,2466,138) rot=(0,0,1;0rad)
  Width = 89
FEATURE [Part::Box] Box001001002001001001003002005003022001003004002001003001004002002001004002003005001001001001001001002001002001001004001001002002001005005002010015002  label="Terrasplank003"
  AttacherType = Attacher::AttachEngine3D
  Height = 15.5
  Length = 3000
  Placement = pos=(0,2555,138) rot=(0,0,1;0rad)
  Width = 89
FEATURE [Part::Box] Box001001002001001001003002005003022001003004002001003001004002002001004002003005001001001001001001002001002001001004001001002002001005005002010015002001  label="Terrasplank004"
  AttacherType = Attacher::AttachEngine3D
  Height = 15.5
  Length = 3000
  Placement = pos=(0,2644,138) rot=(0,0,1;0rad)
  Width = 89
FEATURE [Part::Box] Box001001002001001001003002005003022001003004002001003001004002002001004002003005001001001001001001002001002001001004001001002002001005005002010015002002  label="Terrasplank005"
  AttacherType = Attacher::AttachEngine3D
  Height = 15.5
  Length = 3000
  Placement = pos=(0,2733,138) rot=(0,0,1;0rad)
  Width = 89
FEATURE [Part::Box] Box001001002001001001003002005003022001003004002001003001004002002001004002003005001001001001001001002001002001001004001001002002001005005002010015002003  label="Terrasplank006"
  AttacherType = Attacher::AttachEngine3D
  Height = 15.5
  Length = 3000
  Placement = pos=(0,2822,138) rot=(0,0,1;0rad)
  Width = 89
FEATURE [Part::Box] Box001001002001001001003002005003022001003004002001003001004002002001004002003005001001001001001001002001002001001004001001002002001005005002010015002004  label="Terrasplank007"
  AttacherType = Attacher::AttachEngine3D
  Height = 15.5
  Length = 3000
  Placement = pos=(0,2911,138) rot=(0,0,1;0rad)
  Width = 89
FEATURE [Part::Torus] Torus001001  label="230Vlicht002"
  Angle1 = -180
  Angle2 = 180
  Angle3 = 90
  AttacherType = Attacher::AttachEngine3D
  Placement = pos=(2091,2065,225) rot=(0,1,0;1.5708rad)
  Radius1 = 60
  Radius2 = 11
FEATURE [Part::Torus] Torus001002  label="230Vlight004"
  Angle1 = -180
  Angle2 = 180
  Angle3 = 90
  AttacherType = Attacher::AttachEngine3D
  Placement = pos=(2031,289,165) rot=(0,0,-1;1.5708rad)
  Radius1 = 60
  Radius2 = 11
FEATURE [Part::Mirroring] Part__Mirroring  label="230Vlight006"
  Base = (2000,2000,50)
  Normal = (0,1,0)
  Placement = pos=(-793,2320,1) rot=(0,0,-1;1.5708rad)
  Source = -> Torus001001
FEATURE [Part::Cylinder] Cylinder004  label="230Vlight003"
  Angle = 360
  AttacherType = Attacher::AttachEngine3D
  Height = 1776
  Placement = pos=(2091,2065,165) rot=(1,0,0;1.5708rad)
  Radius = 11
FEATURE [Part::Cylinder] Cylinder005  label="380Vin003"
  Angle = 360
  AttacherType = Attacher::AttachEngine3D
  Height = 745
  Placement = pos=(2091,2045,1680) rot=(0,0,1;0rad)
  Radius = 11
FEATURE [Part::Cylinder] Cylinder005001  label="230Vlight001"
  Angle = 360
  AttacherType = Attacher::AttachEngine3D
  Height = 1440
  Placement = pos=(2091,2125,225) rot=(0,0,1;0rad)
  Radius = 11
FEATURE [Part::Cylinder] Cylinder004001  label="380Vheater003"
  Angle = 360
  AttacherType = Attacher::AttachEngine3D
  Height = 1065
  Placement = pos=(2091,2010,205) rot=(1,0,0;1.5708rad)
  Radius = 11
FEATURE [Part::Torus] Torus001001001  label="380Vheater002"
  Angle1 = -180
  Angle2 = 180
  Angle3 = 90
  AttacherType = Attacher::AttachEngine3D
  Placement = pos=(2091,2010,265) rot=(0,1,0;1.5708rad)
  Radius1 = 60
  Radius2 = 11
FEATURE [Part::Cylinder] Cylinder005001001  label="380Vheater001"
  Angle = 360
  AttacherType = Attacher::AttachEngine3D
  Height = 1400
  Placement = pos=(2091,2070,265) rot=(0,0,1;0rad)
  Radius = 11
FEATURE [Part::Cylinder] Cylinder003001  label="230Vlight005"
  Angle = 360
  AttacherType = Attacher::AttachEngine3D
  Height = 889
  Placement = pos=(1142,229,165) rot=(0,1,0;1.5708rad)
  Radius = 11
FEATURE [Part::Torus] Torus001001002  label="380Vheater005"
  Angle1 = -180
  Angle2 = 180
  Angle3 = 90
  AttacherType = Attacher::AttachEngine3D
  Placement = pos=(2031,885,265) rot=(1,0,0;1.5708rad)
  Radius1 = 60
  Radius2 = 11
FEATURE [Part::Torus] Torus001001003  label="380Vheater006"
  Angle1 = -180
  Angle2 = 180
  Angle3 = 90
  AttacherType = Attacher::AttachEngine3D
  Placement = pos=(2031,825,325) rot=(0,0,1;1.5708rad)
  Radius1 = 60
  Radius2 = 11
FEATURE [Part::Cylinder] Cylinder005001001001  label="230Vlight007"
  Angle = 360
  AttacherType = Attacher::AttachEngine3D
  Height = 1460
  Placement = pos=(1081,228,225) rot=(0,0,1;0rad)
  Radius = 11
FEATURE [Part::Mirroring] Part__Mirroring001  label="380Vheater004"
  Base = (2000,2000,50)
  Normal = (0,1,0)
  Placement = pos=(0,-990,40) rot=(0,0,1;0rad)
  Source = -> Torus001001
FEATURE [Part::Box] Box001001002001001001003002005003022001003004002001003001004002002001004002003005001001001001001001002001002001001004001001002002001005005002010015002005  label="AJ001"
  AttacherType = Attacher::AttachEngine3D
  Height = 2145
  Length = 32
  Placement = pos=(151,168.5,138) rot=(0,0,1;0rad)
  Width = 18
FEATURE [Part::Box] Box001001002001001001003002005003022001003004002001003001004002002001004002003005001001001001001001002001002001001004001001002002001005005002010015002005001  label="AJ002"
  AttacherType = Attacher::AttachEngine3D
  Height = 2145
  Length = 32
  Placement = pos=(755,168.5,138) rot=(0,0,1;0rad)
  Width = 18
FEATURE [Part::Box] Box001001002001001001003002005003022001003004002001003001004002002001004002003005001001001001001001002001002001001004001001002002001005005002010015002005001001  label="AJ003"
  AttacherType = Attacher::AttachEngine3D
  Height = 2145
  Length = 32
  Placement = pos=(1359,168.5,138) rot=(0,0,1;0rad)
  Width = 18
FEATURE [Part::Box] Box001001002001001001003002005003022001003004002001003001004002002001004002003005001001001001001001002001002001001004001001002002001005005002010015002005001001001  label="AJ004"
  AttacherType = Attacher::AttachEngine3D
  Height = 2145
  Length = 32
  Placement = pos=(1948,168.5,138) rot=(0,0,1;0rad)
  Width = 18
FEATURE [Part::Box] Box001001002001001001003002005003022001003004002001003001004002002001004002003005001001001001001001002001002001001004001001002002001005005002010015002005001001001001  label="AJ005"
  AttacherType = Attacher::AttachEngine3D
  Height = 2145
  Length = 18
  Placement = pos=(2134,405,138) rot=(0,0,1;0rad)
  Width = 32
FEATURE [Part::Box] Box001001002001001001003002005003022001003004002001003001004002002001004002003005001001001001001001002001002001001004001001002002001005005002010015002005001001001001001  label="AJ006"
  AttacherType = Attacher::AttachEngine3D
  Height = 2145
  Length = 18
  Placement = pos=(2134,1007,138) rot=(0,0,1;0rad)
  Width = 32
FEATURE [Part::Box] Box001001002001001001003002005003022001003004002001003001004002002001004002003005001001001001001001002001002001001004001001002002001005005002010015002005001001001001001001  label="AJ007"
  AttacherType = Attacher::AttachEngine3D
  Height = 2145
  Length = 18
  Placement = pos=(2134,1669,138) rot=(0,0,1;0rad)
  Width = 32
FEATURE [Part::Box] Box001001002001001001003002005003022001003004002001003001004002002001004002003005001001001001001001002001002001001004001001002002001005005002010015002005001001001001001001001  label="AJ008"
  AttacherType = Attacher::AttachEngine3D
  Height = 2145
  Length = 18
  Placement = pos=(2134,2271,138) rot=(0,0,1;0rad)
  Width = 32
FEATURE [Part::Box] Box001001002001001001003002005003022001003004002001003001004002002001004002003005001001001001001001002001002001001004001001002002001005005002010015002005001001001001001001002  label="left MDF plate"
  AttacherType = Attacher::AttachEngine3D
  Height = 2145
  Length = 2130
  Placement = pos=(0,186.5,138) rot=(0,0,1;0rad)
  Width = 2.5
FEATURE [Part::Box] Box001001002001001001003002005003022001003004002001003001004002002001004002003005001001001001001001002001002001001004001001002002001005005002010015002005001001001001001001003  label="AJ009"
  AttacherType = Attacher::AttachEngine3D
  Height = 2145
  Length = 32
  Placement = pos=(150,2521.5,138) rot=(0,0,1;0rad)
  Width = 18
FEATURE [Part::Box] Box001001002001001001003002005003022001003004002001003001004002002001004002003005001001001001001001002001002001001004001001002002001005005002010015002005001001001001001001004  label="AJ010"
  AttacherType = Attacher::AttachEngine3D
  Height = 2145
  Length = 32
  Placement = pos=(755,2521.5,138) rot=(0,0,1;0rad)
  Width = 18
FEATURE [Part::Box] Box001001002001001001003002005003022001003004002001003001004002002001004002003005001001001001001001002001002001001004001001002002001005005002010015002005001001001001001001005  label="AJ011"
  AttacherType = Attacher::AttachEngine3D
  Height = 2145
  Length = 32
  Placement = pos=(1360,2521.5,138) rot=(0,0,1;0rad)
  Width = 18
FEATURE [Part::Box] Box001001002001001001003002005003022001003004002001003001004002002001004002003005001001001001001001002001002001001004001001002002001005005002010015002005001001001001001001006  label="AJ012"
  AttacherType = Attacher::AttachEngine3D
  Height = 2145
  Length = 32
  Placement = pos=(1948,2521.5,138) rot=(0,0,1;0rad)
  Width = 18
FEATURE [Part::Box] Box001001002001001001003002005003022001003004002001003001004002002001004002003005001001001001001001002001002001001004001001002002001005005002010015002005001001001001001001002001  label="right MDF plate"
  AttacherType = Attacher::AttachEngine3D
  Height = 2145
  Length = 2130
  Placement = pos=(0,2519,138) rot=(0,0,1;0rad)
  Width = 2.5
FEATURE [Part::Box] Box001001002001001001003002005003022001003004002001003001004002002001004002003005001001001001001001002001002001001004001001002002001005005002010015002005001001001001001001002002  label="AJ013"
  AttacherType = Attacher::AttachEngine3D
  Height = 2145
  Length = 18
  Placement = pos=(-20.5,433,138) rot=(0,0,1;0rad)
  Width = 32
FEATURE [Part::Box] Box001001002001001001003002005003022001003004002001003001004002002001004002003005001001001001001001002001002001001004001001002002001005005002010015002005001001001001001001002003  label="AJ014"
  AttacherType = Attacher::AttachEngine3D
  Height = 2145
  Length = 18
  Placement = pos=(-20.5,1038,138) rot=(0,0,1;0rad)
  Width = 32
FEATURE [Part::Box] Box001001002001001001003002005003022001003004002001003001004002002001004002003005001001001001001001002001002001001004001001002002001005005002010015002005001001001001001001002004  label="AJ015"
  AttacherType = Attacher::AttachEngine3D
  Height = 2145
  Length = 18
  Placement = pos=(-20.5,1643,138) rot=(0,0,1;0rad)
  Width = 32
FEATURE [Part::Box] Box001001002001001001003002005003022001003004002001003001004002002001004002003005001001001001001001002001002001001004001001002002001005005002010015002005001001001001001001001001  label="AJ016"
  AttacherType = Attacher::AttachEngine3D
  Height = 2145
  Length = 18
  Placement = pos=(-20.5,2246,138) rot=(0,0,1;0rad)
  Width = 32
FEATURE [Part::Box] Box001001002001001001003002005003022001003004002001003001004002002001004002003005001001001001001001002001002001001004001001002002001005005002010015002005001001001001001001002005  label="rear MDF plate"
  AttacherType = Attacher::AttachEngine3D
  Height = 2145
  Length = 2.5
  Placement = pos=(-2.5,189,138) rot=(0,0,1;0rad)
  Width = 2330
FEATURE [Part::Box] Box001001002001001001003002005003022001003004002001003001004002002001004002003005001001001001001001002001002001001004001001002002001005005002010015002005001001001001001001002005001  label="front MDF plate left"
  AttacherType = Attacher::AttachEngine3D
  Height = 2145
  Length = 4
  Placement = pos=(2130,189,138) rot=(0,0,1;0rad)
  Width = 850
FEATURE [Part::Box] Box001001002001001001003002005003022001003004002001003001004002002001004002003005001001001001001001002001002001001004001001002002001005005002010015002005001001001001001001002005001001  label="front MDF plate right"
  AttacherType = Attacher::AttachEngine3D
  Height = 2145
  Length = 4
  Placement = pos=(2130,1669,138) rot=(0,0,1;0rad)
  Width = 850
FEATURE [Part::Box] Box001001002001001001003002005003022001003004002001003001004002002001004002003005001001001001001001002001002001001004001001002002001005005002010015002005001001001001001001002005001002  label="Terrasbalk004"
  AttacherType = Attacher::AttachEngine3D
  Height = 38
  Length = 58
  Placement = pos=(1470,0,100) rot=(0,0,1;0rad)
  Width = 3000
FEATURE [Part::Box] Box001001002001001001003002005003022001003004002001003001004002002001004002003005001001001001001001002001002001001004001001002002001005005002010015002005001001001001001001002005001003  label="Terrasbalk005"
  AttacherType = Attacher::AttachEngine3D
  Height = 38
  Length = 58
  Placement = pos=(1960,0,100) rot=(0,0,1;0rad)
  Width = 3000
FEATURE [Part::Box] Box001001002001001001003002005003022001003004002001003001004002002001004002003005001001001001001001002001002001001004001001002002001005005002010015002005001001001001001001002005001004  label="Terrasbalk006"
  AttacherType = Attacher::AttachEngine3D
  Height = 38
  Length = 58
  Placement = pos=(2450,0,100) rot=(0,0,1;0rad)
  Width = 3000
FEATURE [Part::Box] Box001001002001001001003002005003022001003004002001003001004002002001004002003005001001001001001001002001002001001004001001002002001005005002010015002005001001001001001001002005001005  label="Terrasbalk007"
  AttacherType = Attacher::AttachEngine3D
  Height = 38
  Length = 58
  Placement = pos=(2940,0,100) rot=(0,0,1;0rad)
  Width = 3000
FEATURE [Part::Box] Box001001002001001001003002005003022001003004002001003001004002002001004002003005001001001001001001002001002001001004001001002002001005005002010015002005001001001001001001002005001006  label="Terrasbalk008"
  AttacherType = Attacher::AttachEngine3D
  Height = 38
  Length = 58
  Placement = pos=(2167,152,100) rot=(0,0,1;0rad)
  Width = 2404
FEATURE [App::DocumentObjectGroup] Group001011  label="Terrace"
  Group = -> [Box001001002001001001003002005003022001003004002001003001004002002001004002003005001001001001001001002001002001001004001001002,Box001001002001001001003002005003022001003004002001003001004002002001004002003005001001001001001001002001002001001004001001002001,Box001001002001001001003002005003022001003004002001003001004002002001004002003005001001001001001001002001002001001004001001002002,+39 more]
FEATURE [Part::Cylinder] Cylinder004002  label="380Vin001"
  Angle = 360
  AttacherType = Attacher::AttachEngine3D
  Height = 900
  Placement = pos=(2091,3000,2440) rot=(1,0,0;1.5708rad)
  Radius = 11
FEATURE [Part::Box] Box001001002001001001003002005003022001003004002001003001004002002001004002003005003005001001002003001  label="J017"
  AttacherType = Attacher::AttachEngine3D
  Height = 25
  Length = 80
  Placement = pos=(759,362,1080) rot=(0,0,1;0rad)
  Width = 1984
FEATURE [Part::Box] Box001001002001001001003002005003022001003004002001003001004002001002  label="Y005"
  AttacherType = Attacher::AttachEngine3D
  Height = 80
  Length = 25
  Placement = pos=(843,362,1025) rot=(0,0,1;0rad)
  Width = 1371
FEATURE [Part::Box] Box001001002001001001003002005003022001003004002001003001004002002001004002003005001001001001001001002001002001001004001001002002001005005002010015002005001001001001001001002005001007  label="Z009"
  AttacherType = Attacher::AttachEngine3D
  Height = 95
  Length = 44
  Placement = pos=(799,357,985) rot=(0,0,1;0rad)
  Width = 1994
FEATURE [Part::Box] Box001001002001001001003002005003022001003004002001003001004002002001004002003005003005001001002003002  label="C007"
  AttacherType = Attacher::AttachEngine3D
  Height = 25
  Length = 1114
  Placement = pos=(843,1762,1080) rot=(0,0,1;0rad)
  Width = 80
FEATURE [Part::Box] Box001001002001001001003002005003022001003004002001003001004002002001004002003005001001001001001001002001002001001004001001002002001005005002010015002005001001001001001001002005001008  label="Z010"
  AttacherType = Attacher::AttachEngine3D
  Height = 95
  Length = 1119
  Placement = pos=(843,1758,985) rot=(0,0,1;0rad)
  Width = 44
FEATURE [Part::Box] Box001001002001001001003002005003022001003004002001003001004002002001004001001  label="C009"
  AttacherType = Attacher::AttachEngine3D
  Height = 80
  Length = 1114
  Placement = pos=(843,1733,941) rot=(0,0,1;0rad)
  Width = 25
FEATURE [Part::Box] Box001001002001001001003002005003022001003004002001003001004002001001001  label="J022"
  AttacherType = Attacher::AttachEngine3D
  Height = 80
  Length = 25
  Placement = pos=(1446,362,521) rot=(0,0,1;0rad)
  Width = 1984
FEATURE [Part::Box] Box001001002001001001003002005003022001003004002001003001004002002001004002003005002001  label="J018"
  AttacherType = Attacher::AttachEngine3D
  Height = 25
  Length = 80
  Placement = pos=(774,362,660) rot=(0,0,1;0rad)
  Width = 1984
FEATURE [Part::Box] Box001001002001001001003002005003022001003004002001003001004002002001002001  label="Y007"
  AttacherType = Attacher::AttachEngine3D
  Height = 95
  Length = 44
  Placement = pos=(1402,357,565) rot=(0,0,1;0rad)
  Width = 1994
FEATURE [Part::Box] Box001001002001001001003002005003022001003004002001003001004002002001004002003005001001001001001001002001002001001003001001  label="AF003"
  AttacherType = Attacher::AttachEngine3D
  Height = 80
  Length = 660
  Placement = pos=(208,372,1445) rot=(0,0,1;0rad)
  Width = 25
FEATURE [Part::Box] Box001001002001001001003002005003022001003004002001003001004002002001004002003005001001001001001001002001002001001003002003  label="AF004"
  AttacherType = Attacher::AttachEngine3D
  Height = 80
  Length = 1739
  Placement = pos=(208,2311,1361) rot=(0,0,1;0rad)
  Width = 25
FEATURE [Part::Box] Box001001002001001001003002005003022001003004002001003001004002002001004001002  label="C008"
  AttacherType = Attacher::AttachEngine3D
  Height = 80
  Length = 1114
  Placement = pos=(843,1733,1025) rot=(0,0,1;0rad)
  Width = 25
FEATURE [Part::Box] Box001001002001001001003002005003022001003004002001003001004002002001004001001001  label="H005"
  AttacherType = Attacher::AttachEngine3D
  Height = 80
  Length = 603
  Placement = pos=(868,372,941) rot=(0,0,1;0rad)
  Width = 25
FEATURE [Part::Box] Box001001002001001001003002005003022001003004002001003001004002002001004002003005001001001001001001002001002001001004001001002002001005005002010015002005001001001001001001002005001009  label="J019"
  AttacherType = Attacher::AttachEngine3D
  Height = 80
  Length = 25
  Placement = pos=(1922,1733,1445) rot=(0,0,1;0rad)
  Width = 578
FEATURE [Part::Box] Box001001002001001001003002005003022001003004002001003001004002002001004002003005001001001001001001002001002001001004001001002002001005005002010015002005001001001001001001002005001010  label="J020"
  AttacherType = Attacher::AttachEngine3D
  Height = 80
  Length = 25
  Placement = pos=(183,372,1361) rot=(0,0,1;0rad)
  Width = 1964
FEATURE [Part::Box] Box001001002001001001003002005003022001003004002001003001004002002001004002003005001001001001001001002001002001001004001001002002001005005002010015002005001001001001001001002005001011  label="OB001"
  AttacherType = Attacher::AttachEngine3D
  Height = 1813
  Length = 21
  Placement = pos=(2074,1039,297.5) rot=(0,0,1;1.5708rad)
  Width = 107
FEATURE [Part::Box] Box002  label="P001"
  AttacherType = Attacher::AttachEngine3D
  Height = 16
  Length = 588
  Placement = pos=(2128.5,1060,297.5) rot=(0,0,1;1.5708rad)
  Width = 94
FEATURE [Part::Box] Box003  label="Q001"
  AttacherType = Attacher::AttachEngine3D
  Height = 1781
  Length = 16
  Placement = pos=(2144,1060,313.5) rot=(0,0,1;1.5708rad)
  Width = 94
FEATURE [Part::Box] Box004  label="R001"
  AttacherType = Attacher::AttachEngine3D
  Height = 16
  Length = 572
  Placement = pos=(2079,1076,313.5) rot=(0,0,1;1.5708rad)
  Width = 44.5
FEATURE [Part::Box] Box005  label="S001"
  AttacherType = Attacher::AttachEngine3D
  Height = 1749
  Length = 16
  Placement = pos=(2079,1076,329.5) rot=(0,0,1;1.5708rad)
  Width = 44.5
FEATURE [Part::Box] Box006  label="T001"
  AttacherType = Attacher::AttachEngine3D
  Height = 1771
  Length = 10
  Placement = pos=(2178,1065,318.5) rot=(0,0,1;1.5708rad)
  Width = 44.5
FEATURE [Part::Box] Box007  label="U001"
  AttacherType = Attacher::AttachEngine3D
  Height = 16
  Length = 578
  Placement = pos=(2178,1065,302.5) rot=(0,0,1;1.5708rad)
  Width = 44.5
FEATURE [Part::Box] Box009  label="W001"
  AttacherType = Attacher::AttachEngine3D
  Height = 16
  Length = 520
  Placement = pos=(2178,1107,318.5) rot=(0,0,1;1.5708rad)
  Width = 94
FEATURE [Part::Box] Box010  label="X001"
  AttacherType = Attacher::AttachEngine3D
  Height = 502
  Length = 16
  Placement = pos=(2178,1188,1466.5) rot=(0,0,1;1.5708rad)
  Width = 94
FEATURE [Part::Box] Box001001002001001001003002005003022001003004002001003001004002002001004002003005001001001001001001002001002001001004001001002002001005005002010015002005001001001001001001002005001012  label="N001"
  AttacherType = Attacher::AttachEngine3D
  Height = 21
  Length = 630
  Placement = pos=(2129,1039,276.5) rot=(0,0,1;1.5708rad)
  Width = 167
FEATURE [Part::Box] Box011  label="N002"
  AttacherType = Attacher::AttachEngine3D
  Height = 21
  Length = 630
  Placement = pos=(2129,1039,2110.5) rot=(0,0,1;1.5708rad)
  Width = 167
FEATURE [Part::Box] Box001001002001001001003002005003022001003004002001003001004002002001004002003005001001001001001001002001002001001004001001002002001005005002010015002005001001001001001001002005001013  label="O002"
  AttacherType = Attacher::AttachEngine3D
  Height = 1813
  Length = 21
  Placement = pos=(2129,1648,297.5) rot=(0,0,1;1.5708rad)
  Width = 167
FEATURE [Part::Box] Box002001  label="P002"
  AttacherType = Attacher::AttachEngine3D
  Height = 16
  Length = 588
  Placement = pos=(2128.5,1060,2094.5) rot=(0,0,1;1.5708rad)
  Width = 94
FEATURE [Part::Box] Box004001  label="R002"
  AttacherType = Attacher::AttachEngine3D
  Height = 16
  Length = 572
  Placement = pos=(2079,1076,2078.5) rot=(0,0,1;1.5708rad)
  Width = 44.5
FEATURE [Part::Box] Box007001  label="U002"
  AttacherType = Attacher::AttachEngine3D
  Height = 16
  Length = 578
  Placement = pos=(2178,1065,2089.5) rot=(0,0,1;1.5708rad)
  Width = 44.5
FEATURE [Part::Box] Box008001  label="V002"
  AttacherType = Attacher::AttachEngine3D
  Height = 1771
  Length = 16
  Placement = pos=(2178,1091,318.5) rot=(0,0,1;1.5708rad)
  Width = 94
FEATURE [Part::Box] Box008001001  label="V003"
  AttacherType = Attacher::AttachEngine3D
  Height = 1771
  Length = 16
  Placement = pos=(2178,1627,318.5) rot=(0,0,1;1.5708rad)
  Width = 94
FEATURE [Part::Box] Box009001  label="W002"
  AttacherType = Attacher::AttachEngine3D
  Height = 16
  Length = 520
  Placement = pos=(2178,1107,2073.5) rot=(0,0,1;1.5708rad)
  Width = 94
FEATURE [Part::Box] Box010001  label="X002"
  AttacherType = Attacher::AttachEngine3D
  Height = 502
  Length = 16
  Placement = pos=(2178,1506,1466.5) rot=(0,0,1;1.5708rad)
  Width = 94
FEATURE [Part::Box] Box009001001  label="W003"
  AttacherType = Attacher::AttachEngine3D
  Height = 16
  Length = 520
  Placement = pos=(2178,1107,1968.5) rot=(0,0,1;1.5708rad)
  Width = 94
FEATURE [Part::Box] Box009001002  label="W004"
  AttacherType = Attacher::AttachEngine3D
  Height = 16
  Length = 520
  Placement = pos=(2178,1107,1450.5) rot=(0,0,1;1.5708rad)
  Width = 94
FEATURE [Part::Cylinder] Cylinder005001001002
  Angle = 360
  AttacherType = Attacher::AttachEngine3D
  Height = 70
  Placement = pos=(2.5,-2.5,0) rot=(0,0,1;0rad)
  Radius = 2.5
FEATURE [Part::Box] Box009001003002002  label="Scharnierplaatje001"
  AttacherType = Attacher::AttachEngine3D
  Height = 70
  Length = 2
  Width = 40
FEATURE [Part::Box] Box009001003002001001  label="Scharnierplaatje002"
  AttacherType = Attacher::AttachEngine3D
  Height = 70
  Length = 2
  Placement = pos=(3,0,0) rot=(0,0,1;0rad)
  Width = 40
FEATURE [Part::MultiFuse] Fusion  label="hinge001"
  Placement = pos=(2173,1643,475.5) rot=(0,0,1;1.5708rad)
  Shapes = -> [Cylinder005001001002,Box009001003002001001,Box009001003002002]
FEATURE [Part::MultiFuse] Fusion001  label="hinge002"
  Placement = pos=(2173,1643,1175.5) rot=(0,0,1;1.5708rad)
  Shapes = -> [Cylinder005001001002,Box009001003002001001,Box009001003002002]
FEATURE [Part::MultiFuse] Fusion002  label="hinge003"
  Placement = pos=(2173,1643,1875.5) rot=(0,0,1;1.5708rad)
  Shapes = -> [Cylinder005001001002,Box009001003002001001,Box009001003002002]
FEATURE [Part::Box] Box001001002001001001003002005003022001003004002001003001004002002001004002003005001001001001001001002001002001001004001001002002001005005002010015002005001001001001001001002005001014  label="schroot-2014-001"
  AttacherType = Attacher::AttachEngine3D
  Height = 86
  Length = 15
  Placement = pos=(153,347,265) rot=(0,0,1;0rad)
  Width = 2014
FEATURE [Part::Box] Box001001002001001001003002005003022001003004002001003001004002002001004002003005001001001001001001002001002001001004001001002002001005005002010015002005001001001001001001002005001014001  label="schroot-2014-002"
  AttacherType = Attacher::AttachEngine3D
  Height = 86
  Length = 15
  Placement = pos=(153,347,351) rot=(0,0,1;0rad)
  Width = 2014
FEATURE [Part::Box] Box001001002001001001003002005003022001003004002001003001004002002001004002003005001001001001001001002001002001001004001001002002001005005002010015002005001001001001001001002005001014002  label="schroot-2014-003"
  AttacherType = Attacher::AttachEngine3D
  Height = 86
  Length = 15
  Placement = pos=(153,347,437) rot=(0,0,1;0rad)
  Width = 2014
FEATURE [Part::Box] Box001001002001001001003002005003022001003004002001003001004002002001004002003005001001001001001001002001002001001004001001002002001005005002010015002005001001001001001001002005001014003  label="schroot-2014-004"
  AttacherType = Attacher::AttachEngine3D
  Height = 86
  Length = 15
  Placement = pos=(153,347,523) rot=(0,0,1;0rad)
  Width = 2014
FEATURE [Part::Box] Box001001002001001001003002005003022001003004002001003001004002002001004002003005001001001001001001002001002001001004001001002002001005005002010015002005001001001001001001002005001014004  label="schroot-2014-005"
  AttacherType = Attacher::AttachEngine3D
  Height = 86
  Length = 15
  Placement = pos=(153,347,609) rot=(0,0,1;0rad)
  Width = 2014
FEATURE [Part::Box] Box001001002001001001003002005003022001003004002001003001004002002001004002003005001001001001001001002001002001001004001001002002001005005002010015002005001001001001001001002005001014005  label="schroot-2014-006"
  AttacherType = Attacher::AttachEngine3D
  Height = 86
  Length = 15
  Placement = pos=(153,347,695) rot=(0,0,1;0rad)
  Width = 2014
FEATURE [Part::Box] Box001001002001001001003002005003022001003004002001003001004002002001004002003005001001001001001001002001002001001004001001002002001005005002010015002005001001001001001001002005001014006  label="schroot-2014-007"
  AttacherType = Attacher::AttachEngine3D
  Height = 86
  Length = 15
  Placement = pos=(153,347,781) rot=(0,0,1;0rad)
  Width = 2014
FEATURE [Part::Box] Box001001002001001001003002005003022001003004002001003001004002002001004002003005001001001001001001002001002001001004001001002002001005005002010015002005001001001001001001002005001014007  label="schroot-2014-008"
  AttacherType = Attacher::AttachEngine3D
  Height = 86
  Length = 15
  Placement = pos=(153,347,867) rot=(0,0,1;0rad)
  Width = 2014
FEATURE [Part::Box] Box001001002001001001003002005003022001003004002001003001004002002001004002003005001001001001001001002001002001001004001001002002001005005002010015002005001001001001001001002005001014008  label="schroot-2014-009"
  AttacherType = Attacher::AttachEngine3D
  Height = 86
  Length = 15
  Placement = pos=(153,347,953) rot=(0,0,1;0rad)
  Width = 2014
FEATURE [Part::Box] Box001001002001001001003002005003022001003004002001003001004002002001004002003005001001001001001001002001002001001004001001002002001005005002010015002005001001001001001001002005001014009  label="schroot-2014-010"
  AttacherType = Attacher::AttachEngine3D
  Height = 86
  Length = 15
  Placement = pos=(153,347,1039) rot=(0,0,1;0rad)
  Width = 2014
FEATURE [Part::Box] Box001001002001001001003002005003022001003004002001003001004002002001004002003005001001001001001001002001002001001004001001002002001005005002010015002005001001001001001001002005001014010  label="schroot-2014-011"
  AttacherType = Attacher::AttachEngine3D
  Height = 86
  Length = 15
  Placement = pos=(153,347,1125) rot=(0,0,1;0rad)
  Width = 2014
FEATURE [Part::Box] Box001001002001001001003002005003022001003004002001003001004002002001004002003005001001001001001001002001002001001004001001002002001005005002010015002005001001001001001001002005001014011  label="schroot-2014-012"
  AttacherType = Attacher::AttachEngine3D
  Height = 86
  Length = 15
  Placement = pos=(153,347,1211) rot=(0,0,1;0rad)
  Width = 2014
FEATURE [Part::Box] Box001001002001001001003002005003022001003004002001003001004002002001004002003005001001001001001001002001002001001004001001002002001005005002010015002005001001001001001001002005001014012  label="schroot-2014-013"
  AttacherType = Attacher::AttachEngine3D
  Height = 86
  Length = 15
  Placement = pos=(153,347,1297) rot=(0,0,1;0rad)
  Width = 2014
FEATURE [Part::Box] Box001001002001001001003002005003022001003004002001003001004002002001004002003005001001001001001001002001002001001004001001002002001005005002010015002005001001001001001001002005001014013  label="schroot-2014-014"
  AttacherType = Attacher::AttachEngine3D
  Height = 86
  Length = 15
  Placement = pos=(153,347,1383) rot=(0,0,1;0rad)
  Width = 2014
FEATURE [Part::Box] Box001001002001001001003002005003022001003004002001003001004002002001004002003005001001001001001001002001002001001004001001002002001005005002010015002005001001001001001001002005001014014  label="schroot-2014-015"
  AttacherType = Attacher::AttachEngine3D
  Height = 86
  Length = 15
  Placement = pos=(153,347,1469) rot=(0,0,1;0rad)
  Width = 2014
FEATURE [Part::Box] Box001001002001001001003002005003022001003004002001003001004002002001004002003005001001001001001001002001002001001004001001002002001005005002010015002005001001001001001001002005001014015  label="schroot-2014-016"
  AttacherType = Attacher::AttachEngine3D
  Height = 86
  Length = 15
  Placement = pos=(153,347,1555) rot=(0,0,1;0rad)
  Width = 2014
FEATURE [Part::Box] Box001001002001001001003002005003022001003004002001003001004002002001004002003005001001001001001001002001002001001004001001002002001005005002010015002005001001001001001001002005001014016  label="schroot-2014-017"
  AttacherType = Attacher::AttachEngine3D
  Height = 86
  Length = 15
  Placement = pos=(153,347,1641) rot=(0,0,1;0rad)
  Width = 2014
FEATURE [Part::Box] Box001001002001001001003002005003022001003004002001003001004002002001004002003005001001001001001001002001002001001004001001002002001005005002010015002005001001001001001001002005001014017  label="schroot-2014-018"
  AttacherType = Attacher::AttachEngine3D
  Height = 86
  Length = 15
  Placement = pos=(153,347,1727) rot=(0,0,1;0rad)
  Width = 2014
FEATURE [Part::Box] Box001001002001001001003002005003022001003004002001003001004002002001004002003005001001001001001001002001002001001004001001002002001005005002010015002005001001001001001001002005001014018  label="schroot-2014-019"
  AttacherType = Attacher::AttachEngine3D
  Height = 86
  Length = 15
  Placement = pos=(153,347,1813) rot=(0,0,1;0rad)
  Width = 2014
FEATURE [Part::Box] Box001001002001001001003002005003022001003004002001003001004002002001004002003005001001001001001001002001002001001004001001002002001005005002010015002005001001001001001001002005001014019  label="schroot-2014-020"
  AttacherType = Attacher::AttachEngine3D
  Height = 86
  Length = 15
  Placement = pos=(153,347,1899) rot=(0,0,1;0rad)
  Width = 2014
FEATURE [Part::Box] Box001001002001001001003002005003022001003004002001003001004002002001004002003005001001001001001001002001002001001004001001002002001005005002010015002005001001001001001001002005001014020  label="schroot-2014-021"
  AttacherType = Attacher::AttachEngine3D
  Height = 86
  Length = 15
  Placement = pos=(153,347,1985) rot=(0,0,1;0rad)
  Width = 2014
FEATURE [Part::Box] Box001001002001001001003002005003022001003004002001003001004002002001004002003005001001001001001001002001002001001004001001002002001005005002010015002005001001001001001001002005001014020001  label="schroot-2014-022"
  AttacherType = Attacher::AttachEngine3D
  Height = 70
  Length = 15
  Placement = pos=(153,347,2071) rot=(0,0,1;0rad)
  Width = 2014
FEATURE [Part::Box] Box001001002001001001003002005003022001003004002001003001004002002001004002003005001001001001001001002001002001001004001001002002001005005002010015002005001001001001001001002005001014020001001  label="schroot-692-001"
  AttacherType = Attacher::AttachEngine3D
  Height = 86
  Length = 15
  Placement = pos=(1962,347,265) rot=(0,0,1;0rad)
  Width = 692
FEATURE [Part::Box] Box001001002001001001003002005003022001003004002001003001004002002001004002003005001001001001001001002001002001001004001001002002001005005002010015002005001001001001001001002005001014020001001001  label="schroot-692-023"
  AttacherType = Attacher::AttachEngine3D
  Height = 86
  Length = 15
  Placement = pos=(1962,1669,265) rot=(0,0,1;0rad)
  Width = 692
FEATURE [Part::Box] Box001001002001001001003002005003022001003004002001003001004002002001004002003005001001001001001001002001002001001004001001002002001005005002010015002005001001001001001001002005001014020001001002  label="schroot-692-002"
  AttacherType = Attacher::AttachEngine3D
  Height = 86
  Length = 15
  Placement = pos=(1962,347,351) rot=(0,0,1;0rad)
  Width = 692
FEATURE [Part::Box] Box001001002001001001003002005003022001003004002001003001004002002001004002003005001001001001001001002001002001001004001001002002001005005002010015002005001001001001001001002005001014020001001003  label="schroot-692-003"
  AttacherType = Attacher::AttachEngine3D
  Height = 86
  Length = 15
  Placement = pos=(1962,347,437) rot=(0,0,1;0rad)
  Width = 692
FEATURE [Part::Box] Box001001002001001001003002005003022001003004002001003001004002002001004002003005001001001001001001002001002001001004001001002002001005005002010015002005001001001001001001002005001014020001001004  label="schroot-692-004"
  AttacherType = Attacher::AttachEngine3D
  Height = 86
  Length = 15
  Placement = pos=(1962,347,523) rot=(0,0,1;0rad)
  Width = 692
FEATURE [Part::Box] Box001001002001001001003002005003022001003004002001003001004002002001004002003005001001001001001001002001002001001004001001002002001005005002010015002005001001001001001001002005001014020001001005  label="schroot-692-005"
  AttacherType = Attacher::AttachEngine3D
  Height = 86
  Length = 15
  Placement = pos=(1962,347,609) rot=(0,0,1;0rad)
  Width = 692
FEATURE [Part::Box] Box001001002001001001003002005003022001003004002001003001004002002001004002003005001001001001001001002001002001001004001001002002001005005002010015002005001001001001001001002005001014020001001006  label="schroot-692-006"
  AttacherType = Attacher::AttachEngine3D
  Height = 86
  Length = 15
  Placement = pos=(1962,347,695) rot=(0,0,1;0rad)
  Width = 692
FEATURE [Part::Box] Box001001002001001001003002005003022001003004002001003001004002002001004002003005001001001001001001002001002001001004001001002002001005005002010015002005001001001001001001002005001014020001001007  label="schroot-692-007"
  AttacherType = Attacher::AttachEngine3D
  Height = 86
  Length = 15
  Placement = pos=(1962,347,781) rot=(0,0,1;0rad)
  Width = 692
FEATURE [Part::Box] Box001001002001001001003002005003022001003004002001003001004002002001004002003005001001001001001001002001002001001004001001002002001005005002010015002005001001001001001001002005001014020001001008  label="schroot-692-008"
  AttacherType = Attacher::AttachEngine3D
  Height = 86
  Length = 15
  Placement = pos=(1962,347,867) rot=(0,0,1;0rad)
  Width = 692
FEATURE [Part::Box] Box001001002001001001003002005003022001003004002001003001004002002001004002003005001001001001001001002001002001001004001001002002001005005002010015002005001001001001001001002005001014020001001009  label="schroot-692-009"
  AttacherType = Attacher::AttachEngine3D
  Height = 86
  Length = 15
  Placement = pos=(1962,347,953) rot=(0,0,1;0rad)
  Width = 692
FEATURE [Part::Box] Box001001002001001001003002005003022001003004002001003001004002002001004002003005001001001001001001002001002001001004001001002002001005005002010015002005001001001001001001002005001014020001001010  label="schroot-692-010"
  AttacherType = Attacher::AttachEngine3D
  Height = 86
  Length = 15
  Placement = pos=(1962,347,1039) rot=(0,0,1;0rad)
  Width = 692
FEATURE [Part::Box] Box001001002001001001003002005003022001003004002001003001004002002001004002003005001001001001001001002001002001001004001001002002001005005002010015002005001001001001001001002005001014020001001011  label="schroot-692-011"
  AttacherType = Attacher::AttachEngine3D
  Height = 86
  Length = 15
  Placement = pos=(1962,347,1125) rot=(0,0,1;0rad)
  Width = 692
FEATURE [Part::Box] Box001001002001001001003002005003022001003004002001003001004002002001004002003005001001001001001001002001002001001004001001002002001005005002010015002005001001001001001001002005001014020001001012  label="schroot-692-012"
  AttacherType = Attacher::AttachEngine3D
  Height = 86
  Length = 15
  Placement = pos=(1962,347,1211) rot=(0,0,1;0rad)
  Width = 692
FEATURE [Part::Box] Box001001002001001001003002005003022001003004002001003001004002002001004002003005001001001001001001002001002001001004001001002002001005005002010015002005001001001001001001002005001014020001001013  label="schroot-692-013"
  AttacherType = Attacher::AttachEngine3D
  Height = 86
  Length = 15
  Placement = pos=(1962,347,1297) rot=(0,0,1;0rad)
  Width = 692
FEATURE [Part::Box] Box001001002001001001003002005003022001003004002001003001004002002001004002003005001001001001001001002001002001001004001001002002001005005002010015002005001001001001001001002005001014020001001014  label="schroot-692-014"
  AttacherType = Attacher::AttachEngine3D
  Height = 86
  Length = 15
  Placement = pos=(1962,347,1383) rot=(0,0,1;0rad)
  Width = 692
FEATURE [Part::Box] Box001001002001001001003002005003022001003004002001003001004002002001004002003005001001001001001001002001002001001004001001002002001005005002010015002005001001001001001001002005001014020001001015  label="schroot-692-015"
  AttacherType = Attacher::AttachEngine3D
  Height = 86
  Length = 15
  Placement = pos=(1962,347,1469) rot=(0,0,1;0rad)
  Width = 692
FEATURE [Part::Box] Box001001002001001001003002005003022001003004002001003001004002002001004002003005001001001001001001002001002001001004001001002002001005005002010015002005001001001001001001002005001014020001001016  label="schroot-692-016"
  AttacherType = Attacher::AttachEngine3D
  Height = 86
  Length = 15
  Placement = pos=(1962,347,1555) rot=(0,0,1;0rad)
  Width = 692
FEATURE [Part::Box] Box001001002001001001003002005003022001003004002001003001004002002001004002003005001001001001001001002001002001001004001001002002001005005002010015002005001001001001001001002005001014020001001017  label="schroot-692-017"
  AttacherType = Attacher::AttachEngine3D
  Height = 86
  Length = 15
  Placement = pos=(1962,347,1641) rot=(0,0,1;0rad)
  Width = 692
FEATURE [Part::Box] Box001001002001001001003002005003022001003004002001003001004002002001004002003005001001001001001001002001002001001004001001002002001005005002010015002005001001001001001001002005001014020001001018  label="schroot-692-018"
  AttacherType = Attacher::AttachEngine3D
  Height = 86
  Length = 15
  Placement = pos=(1962,347,1727) rot=(0,0,1;0rad)
  Width = 692
FEATURE [Part::Box] Box001001002001001001003002005003022001003004002001003001004002002001004002003005001001001001001001002001002001001004001001002002001005005002010015002005001001001001001001002005001014020001001019  label="schroot-692-019"
  AttacherType = Attacher::AttachEngine3D
  Height = 86
  Length = 15
  Placement = pos=(1962,347,1813) rot=(0,0,1;0rad)
  Width = 692
FEATURE [Part::Box] Box001001002001001001003002005003022001003004002001003001004002002001004002003005001001001001001001002001002001001004001001002002001005005002010015002005001001001001001001002005001014020001001020  label="schroot-692-020"
  AttacherType = Attacher::AttachEngine3D
  Height = 86
  Length = 15
  Placement = pos=(1962,347,1899) rot=(0,0,1;0rad)
  Width = 692
FEATURE [Part::Box] Box001001002001001001003002005003022001003004002001003001004002002001004002003005001001001001001001002001002001001004001001002002001005005002010015002005001001001001001001002005001014020001001021  label="schroot-692-021"
  AttacherType = Attacher::AttachEngine3D
  Height = 86
  Length = 15
  Placement = pos=(1962,347,1985) rot=(0,0,1;0rad)
  Width = 692
FEATURE [Part::Box] Box001001002001001001003002005003022001003004002001003001004002002001004002003005001001001001001001002001002001001004001001002002001005005002010015002005001001001001001001002005001014020001001022  label="schroot-692-022"
  AttacherType = Attacher::AttachEngine3D
  Height = 70
  Length = 15
  Placement = pos=(1962,347,2071) rot=(0,0,1;0rad)
  Width = 692
FEATURE [Part::Box] Box001001002001001001003002005003022001003004002001003001004002002001004002003005001001001001001001002001002001001004001001002002001005005002010015002005001001001001001001002005001014020001001001001  label="schroot-692-024"
  AttacherType = Attacher::AttachEngine3D
  Height = 86
  Length = 15
  Placement = pos=(1962,1669,351) rot=(0,0,1;0rad)
  Width = 692
FEATURE [Part::Box] Box001001002001001001003002005003022001003004002001003001004002002001004002003005001001001001001001002001002001001004001001002002001005005002010015002005001001001001001001002005001014020001001001002  label="schroot-692-025"
  AttacherType = Attacher::AttachEngine3D
  Height = 86
  Length = 15
  Placement = pos=(1962,1669,437) rot=(0,0,1;0rad)
  Width = 692
FEATURE [Part::Box] Box001001002001001001003002005003022001003004002001003001004002002001004002003005001001001001001001002001002001001004001001002002001005005002010015002005001001001001001001002005001014020001001001003  label="schroot-692-026"
  AttacherType = Attacher::AttachEngine3D
  Height = 86
  Length = 15
  Placement = pos=(1962,1669,523) rot=(0,0,1;0rad)
  Width = 692
FEATURE [Part::Box] Box001001002001001001003002005003022001003004002001003001004002002001004002003005001001001001001001002001002001001004001001002002001005005002010015002005001001001001001001002005001014020001001001004  label="schroot-692-027"
  AttacherType = Attacher::AttachEngine3D
  Height = 86
  Length = 15
  Placement = pos=(1962,1669,609) rot=(0,0,1;0rad)
  Width = 692
FEATURE [Part::Box] Box001001002001001001003002005003022001003004002001003001004002002001004002003005001001001001001001002001002001001004001001002002001005005002010015002005001001001001001001002005001014020001001001005  label="schroot-692-028"
  AttacherType = Attacher::AttachEngine3D
  Height = 86
  Length = 15
  Placement = pos=(1962,1669,695) rot=(0,0,1;0rad)
  Width = 692
FEATURE [Part::Box] Box001001002001001001003002005003022001003004002001003001004002002001004002003005001001001001001001002001002001001004001001002002001005005002010015002005001001001001001001002005001014020001001001006  label="schroot-692-029"
  AttacherType = Attacher::AttachEngine3D
  Height = 86
  Length = 15
  Placement = pos=(1962,1669,781) rot=(0,0,1;0rad)
  Width = 692
FEATURE [Part::Box] Box001001002001001001003002005003022001003004002001003001004002002001004002003005001001001001001001002001002001001004001001002002001005005002010015002005001001001001001001002005001014020001001001007  label="schroot-692-030"
  AttacherType = Attacher::AttachEngine3D
  Height = 86
  Length = 15
  Placement = pos=(1962,1669,867) rot=(0,0,1;0rad)
  Width = 692
FEATURE [Part::Box] Box001001002001001001003002005003022001003004002001003001004002002001004002003005001001001001001001002001002001001004001001002002001005005002010015002005001001001001001001002005001014020001001001008  label="schroot-692-031"
  AttacherType = Attacher::AttachEngine3D
  Height = 86
  Length = 15
  Placement = pos=(1962,1669,953) rot=(0,0,1;0rad)
  Width = 692
FEATURE [Part::Box] Box001001002001001001003002005003022001003004002001003001004002002001004002003005001001001001001001002001002001001004001001002002001005005002010015002005001001001001001001002005001014020001001001009  label="schroot-692-032"
  AttacherType = Attacher::AttachEngine3D
  Height = 86
  Length = 15
  Placement = pos=(1962,1669,1039) rot=(0,0,1;0rad)
  Width = 692
FEATURE [Part::Box] Box001001002001001001003002005003022001003004002001003001004002002001004002003005001001001001001001002001002001001004001001002002001005005002010015002005001001001001001001002005001014020001001001010  label="schroot-692-033"
  AttacherType = Attacher::AttachEngine3D
  Height = 86
  Length = 15
  Placement = pos=(1962,1669,1125) rot=(0,0,1;0rad)
  Width = 692
FEATURE [Part::Box] Box001001002001001001003002005003022001003004002001003001004002002001004002003005001001001001001001002001002001001004001001002002001005005002010015002005001001001001001001002005001014020001001001011  label="schroot-692-034"
  AttacherType = Attacher::AttachEngine3D
  Height = 86
  Length = 15
  Placement = pos=(1962,1669,1211) rot=(0,0,1;0rad)
  Width = 692
FEATURE [Part::Box] Box001001002001001001003002005003022001003004002001003001004002002001004002003005001001001001001001002001002001001004001001002002001005005002010015002005001001001001001001002005001014020001001001012  label="schroot-692-035"
  AttacherType = Attacher::AttachEngine3D
  Height = 86
  Length = 15
  Placement = pos=(1962,1669,1297) rot=(0,0,1;0rad)
  Width = 692
FEATURE [Part::Box] Box001001002001001001003002005003022001003004002001003001004002002001004002003005001001001001001001002001002001001004001001002002001005005002010015002005001001001001001001002005001014020001001001013  label="schroot-692-036"
  AttacherType = Attacher::AttachEngine3D
  Height = 86
  Length = 15
  Placement = pos=(1962,1669,1383) rot=(0,0,1;0rad)
  Width = 692
FEATURE [Part::Box] Box001001002001001001003002005003022001003004002001003001004002002001004002003005001001001001001001002001002001001004001001002002001005005002010015002005001001001001001001002005001014020001001001014  label="schroot-692-037"
  AttacherType = Attacher::AttachEngine3D
  Height = 86
  Length = 15
  Placement = pos=(1962,1669,1469) rot=(0,0,1;0rad)
  Width = 692
FEATURE [Part::Box] Box001001002001001001003002005003022001003004002001003001004002002001004002003005001001001001001001002001002001001004001001002002001005005002010015002005001001001001001001002005001014020001001001015  label="schroot-692-038"
  AttacherType = Attacher::AttachEngine3D
  Height = 86
  Length = 15
  Placement = pos=(1962,1669,1555) rot=(0,0,1;0rad)
  Width = 692
FEATURE [Part::Box] Box001001002001001001003002005003022001003004002001003001004002002001004002003005001001001001001001002001002001001004001001002002001005005002010015002005001001001001001001002005001014020001001001016  label="schroot-692-039"
  AttacherType = Attacher::AttachEngine3D
  Height = 86
  Length = 15
  Placement = pos=(1962,1669,1641) rot=(0,0,1;0rad)
  Width = 692
FEATURE [Part::Box] Box001001002001001001003002005003022001003004002001003001004002002001004002003005001001001001001001002001002001001004001001002002001005005002010015002005001001001001001001002005001014020001001001017  label="schroot-692-040"
  AttacherType = Attacher::AttachEngine3D
  Height = 86
  Length = 15
  Placement = pos=(1962,1669,1727) rot=(0,0,1;0rad)
  Width = 692
FEATURE [Part::Box] Box001001002001001001003002005003022001003004002001003001004002002001004002003005001001001001001001002001002001001004001001002002001005005002010015002005001001001001001001002005001014020001001001018  label="schroot-692-041"
  AttacherType = Attacher::AttachEngine3D
  Height = 86
  Length = 15
  Placement = pos=(1962,1669,1813) rot=(0,0,1;0rad)
  Width = 692
FEATURE [Part::Box] Box001001002001001001003002005003022001003004002001003001004002002001004002003005001001001001001001002001002001001004001001002002001005005002010015002005001001001001001001002005001014020001001001019  label="schroot-692-042"
  AttacherType = Attacher::AttachEngine3D
  Height = 86
  Length = 15
  Placement = pos=(1962,1669,1899) rot=(0,0,1;0rad)
  Width = 692
FEATURE [Part::Box] Box001001002001001001003002005003022001003004002001003001004002002001004002003005001001001001001001002001002001001004001001002002001005005002010015002005001001001001001001002005001014020001001001020  label="schroot-692-043"
  AttacherType = Attacher::AttachEngine3D
  Height = 86
  Length = 15
  Placement = pos=(1962,1669,1985) rot=(0,0,1;0rad)
  Width = 692
FEATURE [Part::Box] Box001001002001001001003002005003022001003004002001003001004002002001004002003005001001001001001001002001002001001004001001002002001005005002010015002005001001001001001001002005001014020001001001021  label="schroot-692-044"
  AttacherType = Attacher::AttachEngine3D
  Height = 70
  Length = 15
  Placement = pos=(1962,1669,2071) rot=(0,0,1;0rad)
  Width = 692
FEATURE [Part::Box] Box001001002001001001003002005003022001003004002001003001004002002001004002003005001001001001001001002001002001001004001001002002001005005002010015002005001001001001001001002005001014020001001001022  label="schroot-1790-001"
  AttacherType = Attacher::AttachEngine3D
  Height = 86
  Length = 1790
  Placement = pos=(170,342,265) rot=(0,0,1;0rad)
  Width = 15
FEATURE [Part::Box] Box001001002001001001003002005003022001003004002001003001004002002001004002003005001001001001001001002001002001001004001001002002001005005002010015002005001001001001001001002005001014020001001001022001  label="schroot-1790-002"
  AttacherType = Attacher::AttachEngine3D
  Height = 86
  Length = 1790
  Placement = pos=(170,342,351) rot=(0,0,1;0rad)
  Width = 15
FEATURE [Part::Box] Box001001002001001001003002005003022001003004002001003001004002002001004002003005001001001001001001002001002001001004001001002002001005005002010015002005001001001001001001002005001014020001001001022002  label="schroot-1790-003"
  AttacherType = Attacher::AttachEngine3D
  Height = 86
  Length = 1790
  Placement = pos=(170,342,437) rot=(0,0,1;0rad)
  Width = 15
FEATURE [Part::Box] Box001001002001001001003002005003022001003004002001003001004002002001004002003005001001001001001001002001002001001004001001002002001005005002010015002005001001001001001001002005001014020001001001022003  label="schroot-1790-004"
  AttacherType = Attacher::AttachEngine3D
  Height = 86
  Length = 1790
  Placement = pos=(170,342,523) rot=(0,0,1;0rad)
  Width = 15
FEATURE [Part::Box] Box001001002001001001003002005003022001003004002001003001004002002001004002003005001001001001001001002001002001001004001001002002001005005002010015002005001001001001001001002005001014020001001001022004  label="schroot-1790-005"
  AttacherType = Attacher::AttachEngine3D
  Height = 86
  Length = 1790
  Placement = pos=(170,342,609) rot=(0,0,1;0rad)
  Width = 15
FEATURE [Part::Box] Box001001002001001001003002005003022001003004002001003001004002002001004002003005001001001001001001002001002001001004001001002002001005005002010015002005001001001001001001002005001014020001001001022005  label="schroot-1790-006"
  AttacherType = Attacher::AttachEngine3D
  Height = 86
  Length = 1790
  Placement = pos=(170,342,695) rot=(0,0,1;0rad)
  Width = 15
FEATURE [Part::Box] Box001001002001001001003002005003022001003004002001003001004002002001004002003005001001001001001001002001002001001004001001002002001005005002010015002005001001001001001001002005001014020001001001022006  label="schroot-1790-007"
  AttacherType = Attacher::AttachEngine3D
  Height = 86
  Length = 1790
  Placement = pos=(170,342,781) rot=(0,0,1;0rad)
  Width = 15
FEATURE [Part::Box] Box001001002001001001003002005003022001003004002001003001004002002001004002003005001001001001001001002001002001001004001001002002001005005002010015002005001001001001001001002005001014020001001001022007  label="schroot-1790-008"
  AttacherType = Attacher::AttachEngine3D
  Height = 86
  Length = 1790
  Placement = pos=(170,342,867) rot=(0,0,1;0rad)
  Width = 15
FEATURE [Part::Box] Box001001002001001001003002005003022001003004002001003001004002002001004002003005001001001001001001002001002001001004001001002002001005005002010015002005001001001001001001002005001014020001001001022008  label="schroot-1790-009"
  AttacherType = Attacher::AttachEngine3D
  Height = 86
  Length = 1790
  Placement = pos=(170,342,953) rot=(0,0,1;0rad)
  Width = 15
FEATURE [Part::Box] Box001001002001001001003002005003022001003004002001003001004002002001004002003005001001001001001001002001002001001004001001002002001005005002010015002005001001001001001001002005001014020001001001022009  label="schroot-1790-010"
  AttacherType = Attacher::AttachEngine3D
  Height = 86
  Length = 1790
  Placement = pos=(170,342,1039) rot=(0,0,1;0rad)
  Width = 15
FEATURE [Part::Box] Box001001002001001001003002005003022001003004002001003001004002002001004002003005001001001001001001002001002001001004001001002002001005005002010015002005001001001001001001002005001014020001001001022010  label="schroot-1790-011"
  AttacherType = Attacher::AttachEngine3D
  Height = 86
  Length = 1790
  Placement = pos=(170,342,1125) rot=(0,0,1;0rad)
  Width = 15
FEATURE [Part::Box] Box001001002001001001003002005003022001003004002001003001004002002001004002003005001001001001001001002001002001001004001001002002001005005002010015002005001001001001001001002005001014020001001001022011  label="schroot-1790-012"
  AttacherType = Attacher::AttachEngine3D
  Height = 86
  Length = 1790
  Placement = pos=(170,342,1211) rot=(0,0,1;0rad)
  Width = 15
FEATURE [Part::Box] Box001001002001001001003002005003022001003004002001003001004002002001004002003005001001001001001001002001002001001004001001002002001005005002010015002005001001001001001001002005001014020001001001022012  label="schroot-1790-013"
  AttacherType = Attacher::AttachEngine3D
  Height = 86
  Length = 1790
  Placement = pos=(170,342,1297) rot=(0,0,1;0rad)
  Width = 15
FEATURE [Part::Box] Box001001002001001001003002005003022001003004002001003001004002002001004002003005001001001001001001002001002001001004001001002002001005005002010015002005001001001001001001002005001014020001001001022013  label="schroot-1790-014"
  AttacherType = Attacher::AttachEngine3D
  Height = 86
  Length = 1790
  Placement = pos=(170,342,1383) rot=(0,0,1;0rad)
  Width = 15
FEATURE [Part::Box] Box001001002001001001003002005003022001003004002001003001004002002001004002003005001001001001001001002001002001001004001001002002001005005002010015002005001001001001001001002005001014020001001001022014  label="schroot-1790-015"
  AttacherType = Attacher::AttachEngine3D
  Height = 86
  Length = 1790
  Placement = pos=(170,342,1469) rot=(0,0,1;0rad)
  Width = 15
FEATURE [Part::Box] Box001001002001001001003002005003022001003004002001003001004002002001004002003005001001001001001001002001002001001004001001002002001005005002010015002005001001001001001001002005001014020001001001022015  label="schroot-1790-016"
  AttacherType = Attacher::AttachEngine3D
  Height = 86
  Length = 1790
  Placement = pos=(170,342,1555) rot=(0,0,1;0rad)
  Width = 15
FEATURE [Part::Box] Box001001002001001001003002005003022001003004002001003001004002002001004002003005001001001001001001002001002001001004001001002002001005005002010015002005001001001001001001002005001014020001001001022016  label="schroot-1790-017"
  AttacherType = Attacher::AttachEngine3D
  Height = 86
  Length = 1790
  Placement = pos=(170,342,1641) rot=(0,0,1;0rad)
  Width = 15
FEATURE [Part::Box] Box001001002001001001003002005003022001003004002001003001004002002001004002003005001001001001001001002001002001001004001001002002001005005002010015002005001001001001001001002005001014020001001001022017  label="schroot-1790-018"
  AttacherType = Attacher::AttachEngine3D
  Height = 86
  Length = 1790
  Placement = pos=(170,342,1727) rot=(0,0,1;0rad)
  Width = 15
FEATURE [Part::Box] Box001001002001001001003002005003022001003004002001003001004002002001004002003005001001001001001001002001002001001004001001002002001005005002010015002005001001001001001001002005001014020001001001022018  label="schroot-1790-019"
  AttacherType = Attacher::AttachEngine3D
  Height = 86
  Length = 1790
  Placement = pos=(170,342,1813) rot=(0,0,1;0rad)
  Width = 15
FEATURE [Part::Box] Box001001002001001001003002005003022001003004002001003001004002002001004002003005001001001001001001002001002001001004001001002002001005005002010015002005001001001001001001002005001014020001001001022019  label="schroot-1790-020"
  AttacherType = Attacher::AttachEngine3D
  Height = 86
  Length = 1790
  Placement = pos=(170,342,1899) rot=(0,0,1;0rad)
  Width = 15
FEATURE [Part::Box] Box001001002001001001003002005003022001003004002001003001004002002001004002003005001001001001001001002001002001001004001001002002001005005002010015002005001001001001001001002005001014020001001001022020  label="schroot-1790-021"
  AttacherType = Attacher::AttachEngine3D
  Height = 86
  Length = 1790
  Placement = pos=(170,342,1985) rot=(0,0,1;0rad)
  Width = 15
FEATURE [Part::Box] Box001001002001001001003002005003022001003004002001003001004002002001004002003005001001001001001001002001002001001004001001002002001005005002010015002005001001001001001001002005001014020001001001022021  label="schroot-1790-022"
  AttacherType = Attacher::AttachEngine3D
  Height = 70
  Length = 1790
  Placement = pos=(170,342,2071) rot=(0,0,1;0rad)
  Width = 15
FEATURE [Part::Box] Box001001002001001001003002005003022001003004002001003001004002002001004002003005001001001001001001002001002001001004001001002002001005005002010015002005001001001001001001002005001014020001001001022021001  label="schroot-1790-023"
  AttacherType = Attacher::AttachEngine3D
  Height = 86
  Length = 1790
  Placement = pos=(170,2351,265) rot=(0,0,1;0rad)
  Width = 15
FEATURE [Part::Box] Box001001002001001001003002005003022001003004002001003001004002002001004002003005001001001001001001002001002001001004001001002002001005005002010015002005001001001001001001002005001014020001001001022021001001  label="schroot-1790-024"
  AttacherType = Attacher::AttachEngine3D
  Height = 86
  Length = 1790
  Placement = pos=(170,2351,351) rot=(0,0,1;0rad)
  Width = 15
FEATURE [Part::Box] Box001001002001001001003002005003022001003004002001003001004002002001004002003005001001001001001001002001002001001004001001002002001005005002010015002005001001001001001001002005001014020001001001022021001002  label="schroot-1790-025"
  AttacherType = Attacher::AttachEngine3D
  Height = 86
  Length = 1790
  Placement = pos=(170,2351,437) rot=(0,0,1;0rad)
  Width = 15
FEATURE [Part::Box] Box001001002001001001003002005003022001003004002001003001004002002001004002003005001001001001001001002001002001001004001001002002001005005002010015002005001001001001001001002005001014020001001001022021001003  label="schroot-1790-026"
  AttacherType = Attacher::AttachEngine3D
  Height = 86
  Length = 1790
  Placement = pos=(170,2351,523) rot=(0,0,1;0rad)
  Width = 15
FEATURE [Part::Box] Box001001002001001001003002005003022001003004002001003001004002002001004002003005001001001001001001002001002001001004001001002002001005005002010015002005001001001001001001002005001014020001001001022021001004  label="schroot-1790-027"
  AttacherType = Attacher::AttachEngine3D
  Height = 86
  Length = 1790
  Placement = pos=(170,2351,609) rot=(0,0,1;0rad)
  Width = 15
FEATURE [Part::Box] Box001001002001001001003002005003022001003004002001003001004002002001004002003005001001001001001001002001002001001004001001002002001005005002010015002005001001001001001001002005001014020001001001022021001005  label="schroot-1790-028"
  AttacherType = Attacher::AttachEngine3D
  Height = 86
  Length = 1790
  Placement = pos=(170,2351,695) rot=(0,0,1;0rad)
  Width = 15
FEATURE [Part::Box] Box001001002001001001003002005003022001003004002001003001004002002001004002003005001001001001001001002001002001001004001001002002001005005002010015002005001001001001001001002005001014020001001001022021001006  label="schroot-1790-029"
  AttacherType = Attacher::AttachEngine3D
  Height = 86
  Length = 1790
  Placement = pos=(170,2351,781) rot=(0,0,1;0rad)
  Width = 15
FEATURE [Part::Box] Box001001002001001001003002005003022001003004002001003001004002002001004002003005001001001001001001002001002001001004001001002002001005005002010015002005001001001001001001002005001014020001001001022021001007  label="schroot-1790-030"
  AttacherType = Attacher::AttachEngine3D
  Height = 86
  Length = 1790
  Placement = pos=(170,2351,867) rot=(0,0,1;0rad)
  Width = 15
FEATURE [Part::Box] Box001001002001001001003002005003022001003004002001003001004002002001004002003005001001001001001001002001002001001004001001002002001005005002010015002005001001001001001001002005001014020001001001022021001008  label="schroot-1790-031"
  AttacherType = Attacher::AttachEngine3D
  Height = 86
  Length = 1790
  Placement = pos=(170,2351,953) rot=(0,0,1;0rad)
  Width = 15
FEATURE [Part::Box] Box001001002001001001003002005003022001003004002001003001004002002001004002003005001001001001001001002001002001001004001001002002001005005002010015002005001001001001001001002005001014020001001001022021001009  label="schroot-1790-032"
  AttacherType = Attacher::AttachEngine3D
  Height = 86
  Length = 1790
  Placement = pos=(170,2351,1039) rot=(0,0,1;0rad)
  Width = 15
FEATURE [Part::Box] Box001001002001001001003002005003022001003004002001003001004002002001004002003005001001001001001001002001002001001004001001002002001005005002010015002005001001001001001001002005001014020001001001022021001010  label="schroot-1790-033"
  AttacherType = Attacher::AttachEngine3D
  Height = 86
  Length = 1790
  Placement = pos=(170,2351,1125) rot=(0,0,1;0rad)
  Width = 15
FEATURE [Part::Box] Box001001002001001001003002005003022001003004002001003001004002002001004002003005001001001001001001002001002001001004001001002002001005005002010015002005001001001001001001002005001014020001001001022021001011  label="schroot-1790-034"
  AttacherType = Attacher::AttachEngine3D
  Height = 86
  Length = 1790
  Placement = pos=(170,2351,1211) rot=(0,0,1;0rad)
  Width = 15
FEATURE [Part::Box] Box001001002001001001003002005003022001003004002001003001004002002001004002003005001001001001001001002001002001001004001001002002001005005002010015002005001001001001001001002005001014020001001001022021001012  label="schroot-1790-035"
  AttacherType = Attacher::AttachEngine3D
  Height = 86
  Length = 1790
  Placement = pos=(170,2351,1297) rot=(0,0,1;0rad)
  Width = 15
FEATURE [Part::Box] Box001001002001001001003002005003022001003004002001003001004002002001004002003005001001001001001001002001002001001004001001002002001005005002010015002005001001001001001001002005001014020001001001022021001013  label="schroot-1790-036"
  AttacherType = Attacher::AttachEngine3D
  Height = 86
  Length = 1790
  Placement = pos=(170,2351,1383) rot=(0,0,1;0rad)
  Width = 15
FEATURE [Part::Box] Box001001002001001001003002005003022001003004002001003001004002002001004002003005001001001001001001002001002001001004001001002002001005005002010015002005001001001001001001002005001014020001001001022021001014  label="schroot-1790-037"
  AttacherType = Attacher::AttachEngine3D
  Height = 86
  Length = 1790
  Placement = pos=(170,2351,1469) rot=(0,0,1;0rad)
  Width = 15
FEATURE [Part::Box] Box001001002001001001003002005003022001003004002001003001004002002001004002003005001001001001001001002001002001001004001001002002001005005002010015002005001001001001001001002005001014020001001001022021001015  label="schroot-1790-038"
  AttacherType = Attacher::AttachEngine3D
  Height = 86
  Length = 1790
  Placement = pos=(170,2351,1555) rot=(0,0,1;0rad)
  Width = 15
FEATURE [Part::Box] Box001001002001001001003002005003022001003004002001003001004002002001004002003005001001001001001001002001002001001004001001002002001005005002010015002005001001001001001001002005001014020001001001022021001016  label="schroot-1790-039"
  AttacherType = Attacher::AttachEngine3D
  Height = 86
  Length = 1790
  Placement = pos=(170,2351,1641) rot=(0,0,1;0rad)
  Width = 15
FEATURE [Part::Box] Box001001002001001001003002005003022001003004002001003001004002002001004002003005001001001001001001002001002001001004001001002002001005005002010015002005001001001001001001002005001014020001001001022021001017  label="schroot-1790-040"
  AttacherType = Attacher::AttachEngine3D
  Height = 86
  Length = 1790
  Placement = pos=(170,2351,1727) rot=(0,0,1;0rad)
  Width = 15
FEATURE [Part::Box] Box001001002001001001003002005003022001003004002001003001004002002001004002003005001001001001001001002001002001001004001001002002001005005002010015002005001001001001001001002005001014020001001001022021001018  label="schroot-1790-041"
  AttacherType = Attacher::AttachEngine3D
  Height = 86
  Length = 1790
  Placement = pos=(170,2351,1813) rot=(0,0,1;0rad)
  Width = 15
FEATURE [Part::Box] Box001001002001001001003002005003022001003004002001003001004002002001004002003005001001001001001001002001002001001004001001002002001005005002010015002005001001001001001001002005001014020001001001022021001019  label="schroot-1790-042"
  AttacherType = Attacher::AttachEngine3D
  Height = 86
  Length = 1790
  Placement = pos=(170,2351,1899) rot=(0,0,1;0rad)
  Width = 15
FEATURE [Part::Box] Box001001002001001001003002005003022001003004002001003001004002002001004002003005001001001001001001002001002001001004001001002002001005005002010015002005001001001001001001002005001014020001001001022021001020  label="schroot-1790-043"
  AttacherType = Attacher::AttachEngine3D
  Height = 86
  Length = 1790
  Placement = pos=(170,2351,1985) rot=(0,0,1;0rad)
  Width = 15
FEATURE [Part::Box] Box001001002001001001003002005003022001003004002001003001004002002001004002003005001001001001001001002001002001001004001001002002001005005002010015002005001001001001001001002005001014020001001001022021001021  label="schroot-1790-044"
  AttacherType = Attacher::AttachEngine3D
  Height = 70
  Length = 1790
  Placement = pos=(170,2351,2071) rot=(0,0,1;0rad)
  Width = 15
FEATURE [Part::Box] Box001001002001001001003002005003022001003004002001003001004002002001004002003005001001001001001001002001002001001004001001002002001005005002010015002005001001001001001001002005001014020001001001022021001022  label="schroot-2014-023"
  AttacherType = Attacher::AttachEngine3D
  Height = 15
  Length = 86
  Placement = pos=(158,347,2143) rot=(0,0,1;0rad)
  Width = 2014
FEATURE [Part::Box] Box001001002001001001003002005003022001003004002001003001004002002001004002003005001001001001001001002001002001001004001001002002001005005002010015002005001001001001001001002005001014020001001001022021001022001  label="schroot-2014-024"
  AttacherType = Attacher::AttachEngine3D
  Height = 15
  Length = 86
  Placement = pos=(244,347,2143) rot=(0,0,1;0rad)
  Width = 2014
FEATURE [Part::Box] Box001001002001001001003002005003022001003004002001003001004002002001004002003005001001001001001001002001002001001004001001002002001005005002010015002005001001001001001001002005001014020001001001022021001022002  label="schroot-2014-025"
  AttacherType = Attacher::AttachEngine3D
  Height = 15
  Length = 86
  Placement = pos=(330,347,2143) rot=(0,0,1;0rad)
  Width = 2014
FEATURE [Part::Box] Box001001002001001001003002005003022001003004002001003001004002002001004002003005001001001001001001002001002001001004001001002002001005005002010015002005001001001001001001002005001014020001001001022021001022003  label="schroot-2014-026"
  AttacherType = Attacher::AttachEngine3D
  Height = 15
  Length = 86
  Placement = pos=(416,347,2143) rot=(0,0,1;0rad)
  Width = 2014
FEATURE [Part::Box] Box001001002001001001003002005003022001003004002001003001004002002001004002003005001001001001001001002001002001001004001001002002001005005002010015002005001001001001001001002005001014020001001001022021001022004  label="schroot-2014-027"
  AttacherType = Attacher::AttachEngine3D
  Height = 15
  Length = 86
  Placement = pos=(502,347,2143) rot=(0,0,1;0rad)
  Width = 2014
FEATURE [Part::Box] Box001001002001001001003002005003022001003004002001003001004002002001004002003005001001001001001001002001002001001004001001002002001005005002010015002005001001001001001001002005001014020001001001022021001022005  label="schroot-2014-028"
  AttacherType = Attacher::AttachEngine3D
  Height = 15
  Length = 86
  Placement = pos=(588,347,2143) rot=(0,0,1;0rad)
  Width = 2014
FEATURE [Part::Box] Box001001002001001001003002005003022001003004002001003001004002002001004002003005001001001001001001002001002001001004001001002002001005005002010015002005001001001001001001002005001014020001001001022021001022006  label="schroot-2014-029"
  AttacherType = Attacher::AttachEngine3D
  Height = 15
  Length = 86
  Placement = pos=(674,347,2143) rot=(0,0,1;0rad)
  Width = 2014
FEATURE [Part::Box] Box001001002001001001003002005003022001003004002001003001004002002001004002003005001001001001001001002001002001001004001001002002001005005002010015002005001001001001001001002005001014020001001001022021001022007  label="schroot-2014-030"
  AttacherType = Attacher::AttachEngine3D
  Height = 15
  Length = 86
  Placement = pos=(760,347,2143) rot=(0,0,1;0rad)
  Width = 2014
FEATURE [Part::Box] Box001001002001001001003002005003022001003004002001003001004002002001004002003005001001001001001001002001002001001004001001002002001005005002010015002005001001001001001001002005001014020001001001022021001022008  label="schroot-2014-031"
  AttacherType = Attacher::AttachEngine3D
  Height = 15
  Length = 86
  Placement = pos=(846,347,2143) rot=(0,0,1;0rad)
  Width = 2014
FEATURE [Part::Box] Box001001002001001001003002005003022001003004002001003001004002002001004002003005001001001001001001002001002001001004001001002002001005005002010015002005001001001001001001002005001014020001001001022021001022009  label="schroot-2014-032"
  AttacherType = Attacher::AttachEngine3D
  Height = 15
  Length = 86
  Placement = pos=(932,347,2143) rot=(0,0,1;0rad)
  Width = 2014
FEATURE [Part::Box] Box001001002001001001003002005003022001003004002001003001004002002001004002003005001001001001001001002001002001001004001001002002001005005002010015002005001001001001001001002005001014020001001001022021001022010  label="schroot-2014-033"
  AttacherType = Attacher::AttachEngine3D
  Height = 15
  Length = 86
  Placement = pos=(1018,347,2143) rot=(0,0,1;0rad)
  Width = 2014
FEATURE [Part::Box] Box001001002001001001003002005003022001003004002001003001004002002001004002003005001001001001001001002001002001001004001001002002001005005002010015002005001001001001001001002005001014020001001001022021001022011  label="schroot-2014-034"
  AttacherType = Attacher::AttachEngine3D
  Height = 15
  Length = 86
  Placement = pos=(1104,347,2143) rot=(0,0,1;0rad)
  Width = 2014
FEATURE [Part::Box] Box001001002001001001003002005003022001003004002001003001004002002001004002003005001001001001001001002001002001001004001001002002001005005002010015002005001001001001001001002005001014020001001001022021001022012  label="schroot-2014-035"
  AttacherType = Attacher::AttachEngine3D
  Height = 15
  Length = 86
  Placement = pos=(1190,347,2143) rot=(0,0,1;0rad)
  Width = 2014
FEATURE [Part::Box] Box001001002001001001003002005003022001003004002001003001004002002001004002003005001001001001001001002001002001001004001001002002001005005002010015002005001001001001001001002005001014020001001001022021001022013  label="schroot-2014-036"
  AttacherType = Attacher::AttachEngine3D
  Height = 15
  Length = 86
  Placement = pos=(1276,347,2143) rot=(0,0,1;0rad)
  Width = 2014
FEATURE [Part::Box] Box001001002001001001003002005003022001003004002001003001004002002001004002003005001001001001001001002001002001001004001001002002001005005002010015002005001001001001001001002005001014020001001001022021001022014  label="schroot-2014-037"
  AttacherType = Attacher::AttachEngine3D
  Height = 15
  Length = 86
  Placement = pos=(1362,347,2143) rot=(0,0,1;0rad)
  Width = 2014
FEATURE [Part::Box] Box001001002001001001003002005003022001003004002001003001004002002001004002003005001001001001001001002001002001001004001001002002001005005002010015002005001001001001001001002005001014020001001001022021001022015  label="schroot-2014-038"
  AttacherType = Attacher::AttachEngine3D
  Height = 15
  Length = 86
  Placement = pos=(1448,347,2143) rot=(0,0,1;0rad)
  Width = 2014
FEATURE [Part::Box] Box001001002001001001003002005003022001003004002001003001004002002001004002003005001001001001001001002001002001001004001001002002001005005002010015002005001001001001001001002005001014020001001001022021001022015001  label="schroot-2014-039"
  AttacherType = Attacher::AttachEngine3D
  Height = 15
  Length = 86
  Placement = pos=(1534,347,2143) rot=(0,0,1;0rad)
  Width = 2014
FEATURE [Part::Box] Box001001002001001001003002005003022001003004002001003001004002002001004002003005001001001001001001002001002001001004001001002002001005005002010015002005001001001001001001002005001014020001001001022021001022015002  label="schroot-2014-040"
  AttacherType = Attacher::AttachEngine3D
  Height = 15
  Length = 86
  Placement = pos=(1620,347,2143) rot=(0,0,1;0rad)
  Width = 2014
FEATURE [Part::Box] Box001001002001001001003002005003022001003004002001003001004002002001004002003005001001001001001001002001002001001004001001002002001005005002010015002005001001001001001001002005001014020001001001022021001022015003  label="schroot-2014-041"
  AttacherType = Attacher::AttachEngine3D
  Height = 15
  Length = 86
  Placement = pos=(1706,347,2143) rot=(0,0,1;0rad)
  Width = 2014
FEATURE [Part::Box] Box001001002001001001003002005003022001003004002001003001004002002001004002003005001001001001001001002001002001001004001001002002001005005002010015002005001001001001001001002005001014020001001001022021001022015004  label="schroot-2014-042"
  AttacherType = Attacher::AttachEngine3D
  Height = 15
  Length = 86
  Placement = pos=(1792,347,2143) rot=(0,0,1;0rad)
  Width = 2014
FEATURE [Part::Box] Box001001002001001001003002005003022001003004002001003001004002002001004002003005001001001001001001002001002001001004001001002002001005005002010015002005001001001001001001002005001014020001001001022021001022015005  label="schroot-2014-043"
  AttacherType = Attacher::AttachEngine3D
  Height = 15
  Length = 86
  Placement = pos=(1878,347,2143) rot=(0,0,1;0rad)
  Width = 2014
FEATURE [Part::Box] Box001001002001001001003002005003022001003004002001003001004002002001004002003005001001001001001001002001002001001003002004  label="AE007"
  AttacherType = Attacher::AttachEngine3D
  Height = 164
  Length = 95
  Placement = pos=(350,357,1361) rot=(0,0,1;0rad)
  Width = 15
FEATURE [Part::Box] Box001001002001001001003002005003022001003004002001003001004002002001004002003005001001001001001001002001002001001003002004001  label="AE008"
  AttacherType = Attacher::AttachEngine3D
  Height = 164
  Length = 95
  Placement = pos=(700,357,1361) rot=(0,0,1;0rad)
  Width = 15
FEATURE [Part::Box] Box001001002001001001003002005003022001003004002001003001004002002001004002003005001001001001001001002001002001001003002004001001  label="AE009"
  AttacherType = Attacher::AttachEngine3D
  Height = 164
  Length = 95
  Placement = pos=(900,357,941) rot=(0,0,1;0rad)
  Width = 15
FEATURE [Part::Box] Box001001002001001001003002005003022001003004002001003001004002002001004002003005001001001001001001002001002001001003002004001001001  label="AE010"
  AttacherType = Attacher::AttachEngine3D
  Height = 164
  Length = 95
  Placement = pos=(1300,357,941) rot=(0,0,1;0rad)
  Width = 15
FEATURE [Part::Box] Box001001002001001001003002005003022001003004002001003001004002002001004002003005001001001001001001002001002001001002001  label="AE011"
  AttacherType = Attacher::AttachEngine3D
  Height = 164
  Length = 15
  Placement = pos=(1947,2089,1361) rot=(0,0,1;0rad)
  Width = 95
FEATURE [Part::Box] Box001001002001001001003002005003022001003004002001003001004002002001004002003005001001001001001001002001002001001002001001  label="AE012"
  AttacherType = Attacher::AttachEngine3D
  Height = 164
  Length = 15
  Placement = pos=(1947,1800,1361) rot=(0,0,1;0rad)
  Width = 95
FEATURE [Part::Chamfer] Chamfer
  Edges = 1 edges r=20: [Edge11]
FEATURE [Part::Chamfer] Chamfer001
  Base = -> Chamfer
  Edges = 1 edges r=20: [Edge11]
FEATURE [Part::Chamfer] Chamfer002
  Base = -> Chamfer001
  Edges = 1 edges r=20: [Edge5]
FEATURE [Part::Chamfer] Chamfer003
  Base = -> Chamfer002
  Edges = 1 edges r=20: [Edge5]
FEATURE [Part::Chamfer] Chamfer004
  Base = -> Chamfer003
  Edges = 1 edges r=20: [Edge20]
FEATURE [Part::Chamfer] Chamfer005
  Base = -> Chamfer004
  Edges = 1 edges r=20: [Edge17]
FEATURE [Part::Chamfer] Chamfer006
  Base = -> Chamfer005
  Edges = 1 edges r=20: [Edge18]
FEATURE [Part::Cylinder] Cylinder005001001003
  Angle = 360
  AttacherType = Attacher::AttachEngine3D
  Height = 15
  Placement = pos=(2232,2046,1733) rot=(0,1,0;1.5708rad)
  Radius = 15
FEATURE [Part::Cylinder] Cylinder005001001003001
  Angle = 360
  AttacherType = Attacher::AttachEngine3D
  Height = 15
  Placement = pos=(2232,2106,1733) rot=(0,1,0;1.5708rad)
  Radius = 15
FEATURE [Part::Cylinder] Cylinder005001001003002
  Angle = 360
  AttacherType = Attacher::AttachEngine3D
  Height = 15
  Placement = pos=(2232,2167,1733) rot=(0,1,0;1.5708rad)
  Radius = 15
FEATURE [Part::MultiFuse] Fusion003  label="Controller"
  Placement = pos=(8,0,0) rot=(0,0,1;0rad)
  Shapes = -> [Chamfer006,Cylinder005001001003,Cylinder005001001003001,Cylinder005001001003002]
FEATURE [Part::Box] Box003001  label="Q002"
  AttacherType = Attacher::AttachEngine3D
  Height = 1781
  Length = 16
  Placement = pos=(2144,1070,313.5) rot=(0,0,1;1.44862rad)
  Width = 94
FEATURE [Part::Cut] Cut
  Base = -> Box003
  Placement = pos=(-15.5,0,0) rot=(0,0,1;0rad)
  Tool = -> Box003001
FEATURE [Part::Box] Box008001002  label="V004"
  AttacherType = Attacher::AttachEngine3D
  Height = 1771
  Length = 16
  Placement = pos=(2146,1055.3,318.5) rot=(0,0,1;1.44862rad)
  Width = 94
FEATURE [Part::Cut] Cut001
  Placement = pos=(29,0,0) rot=(0,0,1;0rad)
  Tool = -> Box008001002
FEATURE [Part::Box] Box001001002001001001003002005003022001003004002001003001004002002001004002003005001001001001001001002001002001001004001001002002001005005002010015002005001001001001001001002005001013001  label="OA003"
  AttacherType = Attacher::AttachEngine3D
  Height = 1813
  Length = 21
  Placement = pos=(2173,1648,297.5) rot=(0,0,1;1.5708rad)
  Width = 44
FEATURE [Part::Box] Box001001002001001001003002005003022001003004002001003001004002002001004002003005001001001001001001002001002001001004001001002002001005005002010015002005001001001001001001002005001014020001001001022021001022015006  label="Window"
  AttacherType = Attacher::AttachEngine3D
  Height = 500
  Length = 12
  Placement = pos=(2100,1205,1467.5) rot=(0,0,1;0rad)
  Width = 300
FEATURE [Part::Box] Box001001002001001001003002005003022001003004002001003001004002002001004002003005001001001001001001002001002001001004001001002002001005005002010015002005001001001001001001002005001014020001001001022021001022015006002  label="schroot-520-001"
  AttacherType = Attacher::AttachEngine3D
  Height = 86
  Length = 15
  Placement = pos=(2084,1107,334.5) rot=(0,0,1;0rad)
  Width = 520
FEATURE [Part::Box] Box001001002001001001003002005003022001003004002001003001004002002001004002003005001001001001001001002001002001001004001001002002001005005002010015002005001001001001001001002005001014020001001001022021001022015006002001  label="schroot-520-002"
  AttacherType = Attacher::AttachEngine3D
  Height = 86
  Length = 15
  Placement = pos=(2084,1107,420.5) rot=(0,0,1;0rad)
  Width = 520
FEATURE [Part::Box] Box001001002001001001003002005003022001003004002001003001004002002001004002003005001001001001001001002001002001001004001001002002001005005002010015002005001001001001001001002005001014020001001001022021001022015006002002  label="schroot-520-003"
  AttacherType = Attacher::AttachEngine3D
  Height = 86
  Length = 15
  Placement = pos=(2084,1107,506.5) rot=(0,0,1;0rad)
  Width = 520
FEATURE [Part::Box] Box001001002001001001003002005003022001003004002001003001004002002001004002003005001001001001001001002001002001001004001001002002001005005002010015002005001001001001001001002005001014020001001001022021001022015006002003  label="schroot-520-004"
  AttacherType = Attacher::AttachEngine3D
  Height = 86
  Length = 15
  Placement = pos=(2084,1107,592.5) rot=(0,0,1;0rad)
  Width = 520
FEATURE [Part::Box] Box001001002001001001003002005003022001003004002001003001004002002001004002003005001001001001001001002001002001001004001001002002001005005002010015002005001001001001001001002005001014020001001001022021001022015006002004  label="schroot-520-005"
  AttacherType = Attacher::AttachEngine3D
  Height = 86
  Length = 15
  Placement = pos=(2084,1107,678.5) rot=(0,0,1;0rad)
  Width = 520
FEATURE [Part::Box] Box001001002001001001003002005003022001003004002001003001004002002001004002003005001001001001001001002001002001001004001001002002001005005002010015002005001001001001001001002005001014020001001001022021001022015006002005  label="schroot-520-006"
  AttacherType = Attacher::AttachEngine3D
  Height = 86
  Length = 15
  Placement = pos=(2084,1107,764.5) rot=(0,0,1;0rad)
  Width = 520
FEATURE [Part::Box] Box001001002001001001003002005003022001003004002001003001004002002001004002003005001001001001001001002001002001001004001001002002001005005002010015002005001001001001001001002005001014020001001001022021001022015006002006  label="schroot-520-007"
  AttacherType = Attacher::AttachEngine3D
  Height = 86
  Length = 15
  Placement = pos=(2084,1107,850.5) rot=(0,0,1;0rad)
  Width = 520
FEATURE [Part::Box] Box001001002001001001003002005003022001003004002001003001004002002001004002003005001001001001001001002001002001001004001001002002001005005002010015002005001001001001001001002005001014020001001001022021001022015006002007  label="schroot-520-008"
  AttacherType = Attacher::AttachEngine3D
  Height = 86
  Length = 15
  Placement = pos=(2084,1107,936.5) rot=(0,0,1;0rad)
  Width = 520
FEATURE [Part::Box] Box001001002001001001003002005003022001003004002001003001004002002001004002003005001001001001001001002001002001001004001001002002001005005002010015002005001001001001001001002005001014020001001001022021001022015006002008  label="schroot-520-009"
  AttacherType = Attacher::AttachEngine3D
  Height = 86
  Length = 15
  Placement = pos=(2084,1107,1022.5) rot=(0,0,1;0rad)
  Width = 520
FEATURE [Part::Box] Box001001002001001001003002005003022001003004002001003001004002002001004002003005001001001001001001002001002001001004001001002002001005005002010015002005001001001001001001002005001014020001001001022021001022015006002009  label="schroot-520-010"
  AttacherType = Attacher::AttachEngine3D
  Height = 86
  Length = 15
  Placement = pos=(2084,1107,1108.5) rot=(0,0,1;0rad)
  Width = 520
FEATURE [Part::Box] Box001001002001001001003002005003022001003004002001003001004002002001004002003005001001001001001001002001002001001004001001002002001005005002010015002005001001001001001001002005001014020001001001022021001022015006002010  label="schroot-520-011"
  AttacherType = Attacher::AttachEngine3D
  Height = 86
  Length = 15
  Placement = pos=(2084,1107,1194.5) rot=(0,0,1;0rad)
  Width = 520
FEATURE [Part::Box] Box001001002001001001003002005003022001003004002001003001004002002001004002003005001001001001001001002001002001001004001001002002001005005002010015002005001001001001001001002005001014020001001001022021001022015006002011  label="schroot-520-012"
  AttacherType = Attacher::AttachEngine3D
  Height = 86
  Length = 15
  Placement = pos=(2084,1107,1280.5) rot=(0,0,1;0rad)
  Width = 520
FEATURE [Part::Box] Box001001002001001001003002005003022001003004002001003001004002002001004002003005001001001001001001002001002001001004001001002002001005005002010015002005001001001001001001002005001014020001001001022021001022015006002012  label="schroot-520-013"
  AttacherType = Attacher::AttachEngine3D
  Height = 86
  Length = 15
  Placement = pos=(2084,1107,1366.5) rot=(0,0,1;0rad)
  Width = 520
FEATURE [Part::Box] Box001001002001001001003002005003022001003004002001003001004002002001004002003005001001001001001001002001002001001004001001002002001005005002010015002005001001001001001001002005001014020001001001022021001022015006002013  label="schroot-81-001"
  AttacherType = Attacher::AttachEngine3D
  Height = 86
  Length = 15
  Placement = pos=(2084,1107,1452.5) rot=(0,0,1;0rad)
  Width = 81
FEATURE [Part::Box] Box001001002001001001003002005003022001003004002001003001004002002001004002003005001001001001001001002001002001001004001001002002001005005002010015002005001001001001001001002005001014020001001001022021001022015006002014  label="schroot-81-002"
  AttacherType = Attacher::AttachEngine3D
  Height = 86
  Length = 15
  Placement = pos=(2084,1107,1538.5) rot=(0,0,1;0rad)
  Width = 81
FEATURE [Part::Box] Box001001002001001001003002005003022001003004002001003001004002002001004002003005001001001001001001002001002001001004001001002002001005005002010015002005001001001001001001002005001014020001001001022021001022015006002014001  label="schroot-81-003"
  AttacherType = Attacher::AttachEngine3D
  Height = 86
  Length = 15
  Placement = pos=(2084,1107,1624.5) rot=(0,0,1;0rad)
  Width = 81
FEATURE [Part::Box] Box001001002001001001003002005003022001003004002001003001004002002001004002003005001001001001001001002001002001001004001001002002001005005002010015002005001001001001001001002005001014020001001001022021001022015006002014002  label="schroot-81-004"
  AttacherType = Attacher::AttachEngine3D
  Height = 86
  Length = 15
  Placement = pos=(2084,1107,1710.5) rot=(0,0,1;0rad)
  Width = 81
FEATURE [Part::Box] Box001001002001001001003002005003022001003004002001003001004002002001004002003005001001001001001001002001002001001004001001002002001005005002010015002005001001001001001001002005001014020001001001022021001022015006002014003  label="schroot-81-005"
  AttacherType = Attacher::AttachEngine3D
  Height = 86
  Length = 15
  Placement = pos=(2084,1107,1796.5) rot=(0,0,1;0rad)
  Width = 81
FEATURE [Part::Box] Box001001002001001001003002005003022001003004002001003001004002002001004002003005001001001001001001002001002001001004001001002002001005005002010015002005001001001001001001002005001014020001001001022021001022015006002014004  label="schroot-81-006"
  AttacherType = Attacher::AttachEngine3D
  Height = 86
  Length = 15
  Placement = pos=(2084,1107,1882.5) rot=(0,0,1;0rad)
  Width = 81
FEATURE [Part::Box] Box001001002001001001003002005003022001003004002001003001004002002001004002003005001001001001001001002001002001001004001001002002001005005002010015002005001001001001001001002005001014020001001001022021001022015006002014005  label="schroot-520-014"
  AttacherType = Attacher::AttachEngine3D
  Height = 86
  Length = 15
  Placement = pos=(2084,1107,1968.5) rot=(0,0,1;0rad)
  Width = 520
FEATURE [Part::Box] Box001001002001001001003002005003022001003004002001003001004002002001004002003005001001001001001001002001002001001004001001002002001005005002010015002005001001001001001001002005001014020001001001022021001022015006002014005001  label="schroot-520-015"
  AttacherType = Attacher::AttachEngine3D
  Height = 19
  Length = 15
  Placement = pos=(2084,1107,2054.5) rot=(0,0,1;0rad)
  Width = 520
FEATURE [Part::Box] Box001001002001001001003002005003022001003004002001003001004002002001004002003005001001001001001001002001002001001004001001002002001005005002010015002005001001001001001001002005001014020001001001022021001022015006002013001  label="schroot-105-001"
  AttacherType = Attacher::AttachEngine3D
  Height = 86
  Length = 15
  Placement = pos=(2084,1522,1452.5) rot=(0,0,1;0rad)
  Width = 105
FEATURE [Part::Box] Box001001002001001001003002005003022001003004002001003001004002002001004002003005001001001001001001002001002001001004001001002002001005005002010015002005001001001001001001002005001014020001001001022021001022015006002013001001  label="schroot-105-002"
  AttacherType = Attacher::AttachEngine3D
  Height = 86
  Length = 15
  Placement = pos=(2084,1522,1538.5) rot=(0,0,1;0rad)
  Width = 105
FEATURE [Part::Box] Box001001002001001001003002005003022001003004002001003001004002002001004002003005001001001001001001002001002001001004001001002002001005005002010015002005001001001001001001002005001014020001001001022021001022015006002013001002  label="schroot-105-003"
  AttacherType = Attacher::AttachEngine3D
  Height = 86
  Length = 15
  Placement = pos=(2084,1522,1624.5) rot=(0,0,1;0rad)
  Width = 105
FEATURE [Part::Box] Box001001002001001001003002005003022001003004002001003001004002002001004002003005001001001001001001002001002001001004001001002002001005005002010015002005001001001001001001002005001014020001001001022021001022015006002013001003  label="schroot-105-004"
  AttacherType = Attacher::AttachEngine3D
  Height = 86
  Length = 15
  Placement = pos=(2084,1522,1710.5) rot=(0,0,1;0rad)
  Width = 105
FEATURE [Part::Box] Box001001002001001001003002005003022001003004002001003001004002002001004002003005001001001001001001002001002001001004001001002002001005005002010015002005001001001001001001002005001014020001001001022021001022015006002013001004  label="schroot-105-005"
  AttacherType = Attacher::AttachEngine3D
  Height = 86
  Length = 15
  Placement = pos=(2084,1522,1796.5) rot=(0,0,1;0rad)
  Width = 105
FEATURE [Part::Box] Box001001002001001001003002005003022001003004002001003001004002002001004002003005001001001001001001002001002001001004001001002002001005005002010015002005001001001001001001002005001014020001001001022021001022015006002013001005  label="schroot-105-006"
  AttacherType = Attacher::AttachEngine3D
  Height = 86
  Length = 15
  Placement = pos=(2084,1522,1882.5) rot=(0,0,1;0rad)
  Width = 105
FEATURE [Part::Box] Box001001002001001001003002005003022001003004002001003001004002002001004002003005001001001001001001002001002001001004001001002002001005005002010015002005001001001001001001002005001011001  label="OC003"
  AttacherType = Attacher::AttachEngine3D
  Height = 1813
  Length = 21
  Placement = pos=(2173,1039,297.5) rot=(0,0,1;1.5708rad)
  Width = 60
FEATURE [Part::Box] Box001001002001001001003002005003022001003004002001003001004002002001004002003005001001001001001001002001002001001004001001002002001005005002010015002005001001001001001001002005001014020001001001022021001022015006002014005002
  AttacherType = Attacher::AttachEngine3D
  Height = 1835
  Length = 4
  Placement = pos=(2178,1049,286.5) rot=(0,0,1;0rad)
  Width = 594
FEATURE [Part::Box] Box001001002001001001003002005003022001003004002001003001004002002001004002003005001001001001001001002001002001001004001001002002001005005002010015002005001001001001001001002005001014020001001001022021001022015006002014005003  label="Vensterglas001"
  AttacherType = Attacher::AttachEngine3D
  Height = 500
  Length = 100
  Placement = pos=(2106,1205,1467.5) rot=(0,0,1;0rad)
  Width = 300
FEATURE [Part::Cut] Cut002001  label="door MDF plate"
  Base = -> Box001001002001001001003002005003022001003004002001003001004002002001004002003005001001001001001001002001002001001004001001002002001005005002010015002005001001001001001001002005001014020001001001022021001022015006002014005002
  Tool = -> Box001001002001001001003002005003022001003004002001003001004002002001004002003005001001001001001001002001002001001004001001002002001005005002010015002005001001001001001001002005001014020001001001022021001022015006002014005003
FEATURE [Part::Box] Box001001002001001001003002005003022001003004002001003001004002002001004002003005001001001001001001002001002001001004001001002002001005005002010015002005001001001001001001002005001014020001001001022021001022015006002014005004
  AttacherType = Attacher::AttachEngine3D
  Height = 1835
  Length = 15
  Placement = pos=(2182,1049,286.5) rot=(0,0,1;0rad)
  Width = 594
FEATURE [Part::Box] Box001001002001001001003002005003022001003004002001003001004002002001004002003005001001001001001001002001002001001004001001002002001005005002010015002005001001001001001001002005001014020001001001022021001022015006002014005003001  label="Vensterglas002"
  AttacherType = Attacher::AttachEngine3D
  Height = 500
  Length = 100
  Placement = pos=(2126,1205,1467.5) rot=(0,0,1;0rad)
  Width = 300
FEATURE [Part::Cut] Cut002002  label="door finish external"
  Base = -> Box001001002001001001003002005003022001003004002001003001004002002001004002003005001001001001001001002001002001001004001001002002001005005002010015002005001001001001001001002005001014020001001001022021001022015006002014005004
  Tool = -> Box001001002001001001003002005003022001003004002001003001004002002001004002003005001001001001001001002001002001001004001001002002001005005002010015002005001001001001001001002005001014020001001001022021001022015006002014005003001
FEATURE [Part::Box] Box001001002001001001003002005003022001003004002001003001004002002001004002003005001001001001001001002001002001001004001001002002001005005002010015002005001001001001001001002005001014020001001001022021001022015006002014005003002
  AttacherType = Attacher::AttachEngine3D
  Height = 2145
  Length = 19
  Placement = pos=(2152,149.5,138) rot=(0,0,1;0rad)
  Width = 2409
FEATURE [Part::Box] Box001001002001001001003002005003022001003004002001003001004002002001004002003005001001001001001001002001002001001004001001002002001005005002010015002005001001001001001001002005001014020001001001022021001022015006002014005003003
  AttacherType = Attacher::AttachEngine3D
  Height = 1855
  Length = 100
  Placement = pos=(2150,1039,276.5) rot=(0,0,1;0rad)
  Width = 630
FEATURE [Part::Cut] Cut002003  label="front finish external"
  Base = -> Box001001002001001001003002005003022001003004002001003001004002002001004002003005001001001001001001002001002001001004001001002002001005005002010015002005001001001001001001002005001014020001001001022021001022015006002014005003002
  Tool = -> Box001001002001001001003002005003022001003004002001003001004002002001004002003005001001001001001001002001002001001004001001002002001005005002010015002005001001001001001001002005001014020001001001022021001022015006002014005003003
FEATURE [Part::Box] Box001001002001001001003002005003022001003004002001003001004002002001004002003005001001001001001001002001002001001004001001002002001005005002010015002005001001001001001001002005001014020001001001022021001022015006002014005003002001  label="rear finish external"
  AttacherType = Attacher::AttachEngine3D
  Height = 2145
  Length = 19
  Placement = pos=(-39.5,149.5,138) rot=(0,0,1;0rad)
  Width = 2409
FEATURE [Part::Box] Box001001002001001001003002005003022001003004002001003001004002002001004002003005001001001001001001002001002001001004001001002002001005005002010015002005001001001001001001002005001014020001001001022021001022015006002014005003002001001  label="left finish external"
  AttacherType = Attacher::AttachEngine3D
  Height = 2145
  Length = 2172.5
  Placement = pos=(-20.5,149.5,138) rot=(0,0,1;0rad)
  Width = 19
FEATURE [Part::Box] Box001001002001001001003002005003022001003004002001003001004002002001004002003005001001001001001001002001002001001004001001002002001005005002010015002005001001001001001001002005001014020001001001022021001022015006002014005003002001001001  label="right finish external"
  AttacherType = Attacher::AttachEngine3D
  Height = 2145
  Length = 2172.5
  Placement = pos=(-20.5,2539.5,138) rot=(0,0,1;0rad)
  Width = 19
FEATURE [Part::Box] Box001001002001001001003002005003022001003004002001003001004002002001004002003005001001001001001001002001002001001004001001002002001005005002010015002005001001001001001001002005001014020001001001022021001022015006002014005003002001001002  label="front MDF plate bottom"
  AttacherType = Attacher::AttachEngine3D
  Height = 138.5
  Length = 4
  Placement = pos=(2130,1039,138) rot=(0,0,1;0rad)
  Width = 630
FEATURE [Part::Box] Box001001002001001001003002005003022001003004002001003001004002002001004002003005001001001001001001002001002001001004001001002002001005005002010015002005001001001001001001002005001014020001001001022021001022015006002014005003002001001002001  label="front MDF plate top"
  AttacherType = Attacher::AttachEngine3D
  Height = 138.5
  Length = 4
  Placement = pos=(2130,1039,2131.5) rot=(0,0,1;0rad)
  Width = 630
FEATURE [Part::Box] Box001001002001001001003002006  label="A001"
  AttacherType = Attacher::AttachEngine3D
  Height = 100
  Length = 27.5
  Placement = pos=(2.031e-07,189,150) rot=(0,0,1;0rad)
  Width = 2330
FEATURE [Part::Box] Box001001002001001001003002001001  label="A002"
  AttacherType = Attacher::AttachEngine3D
  Height = 100
  Length = 27.5
  Placement = pos=(2102.5,189,150) rot=(0,0,1;0rad)
  Width = 2330
FEATURE [Part::Box] Box001001002001001001003002005001  label="B001"
  AttacherType = Attacher::AttachEngine3D
  Height = 100
  Length = 2075
  Placement = pos=(27.5,2491.5,150) rot=(0,0,1;0rad)
  Width = 27
FEATURE [Part::Box] Box001001002001001001003002004001  label="B002"
  AttacherType = Attacher::AttachEngine3D
  Height = 100
  Length = 2075
  Placement = pos=(27.5,2249,150) rot=(0,0,1;0rad)
  Width = 27
FEATURE [Part::Box] Box001001002001001001003002003001  label="B003"
  AttacherType = Attacher::AttachEngine3D
  Height = 100
  Length = 2075
  Placement = pos=(27.5,1644,150) rot=(0,0,1;0rad)
  Width = 27
FEATURE [Part::Box] Box001001002001001001003001001  label="B004"
  AttacherType = Attacher::AttachEngine3D
  Height = 100
  Length = 2075
  Placement = pos=(27.5,434,150) rot=(0,0,1;0rad)
  Width = 27
FEATURE [Part::Box] Box001001002001001001003002002001  label="B005"
  AttacherType = Attacher::AttachEngine3D
  Height = 100
  Length = 2075
  Placement = pos=(27.5,1039,150) rot=(0,0,1;0rad)
  Width = 27.5
FEATURE [Part::Box] Box001001002001001001003002005002  label="B006"
  AttacherType = Attacher::AttachEngine3D
  Height = 100
  Length = 2075
  Placement = pos=(27.5,189,150) rot=(0,0,1;0rad)
  Width = 27.5
FEATURE [Part::Box] Box001001002001001001003002005003021001  label="base OSB plate"
  AttacherType = Attacher::AttachEngine3D
  Height = 12
  Length = 2130
  Placement = pos=(2.031e-07,189,138) rot=(0,0,1;0rad)
  Width = 2330
FEATURE [Part::Box] Box001001002001001001003002005003  label="Vloerplank001"
  AttacherType = Attacher::AttachEngine3D
  Height = 15
  Length = 89
  Placement = pos=(192,347,250) rot=(0,0,1;0rad)
  Width = 2014
FEATURE [Part::Box] Box001001002001001001003002005003001  label="Vloerplank002"
  AttacherType = Attacher::AttachEngine3D
  Height = 15
  Length = 89
  Placement = pos=(281,347,250) rot=(0,0,1;0rad)
  Width = 2014
FEATURE [Part::Box] Box001001002001001001003002005003002  label="Vloerplank003"
  AttacherType = Attacher::AttachEngine3D
  Height = 15
  Length = 89
  Placement = pos=(370,347,250) rot=(0,0,1;0rad)
  Width = 2014
FEATURE [Part::Box] Box001001002001001001003002005003003  label="Vloerplank004"
  AttacherType = Attacher::AttachEngine3D
  Height = 15
  Length = 89
  Placement = pos=(459,347,250) rot=(0,0,1;0rad)
  Width = 2014
FEATURE [Part::Box] Box001001002001001001003002005003004  label="Vloerplank005"
  AttacherType = Attacher::AttachEngine3D
  Height = 15
  Length = 89
  Placement = pos=(548,347,250) rot=(0,0,1;0rad)
  Width = 2014
FEATURE [Part::Box] Box001001002001001001003002005003005  label="Vloerplank006"
  AttacherType = Attacher::AttachEngine3D
  Height = 15
  Length = 89
  Placement = pos=(637,347,250) rot=(0,0,1;0rad)
  Width = 2014
FEATURE [Part::Box] Box001001002001001001003002005003006  label="Vloerplank007"
  AttacherType = Attacher::AttachEngine3D
  Height = 15
  Length = 89
  Placement = pos=(726,347,250) rot=(0,0,1;0rad)
  Width = 2014
FEATURE [Part::Box] Box001001002001001001003002005003007  label="Vloerplank008"
  AttacherType = Attacher::AttachEngine3D
  Height = 15
  Length = 89
  Placement = pos=(815,347,250) rot=(0,0,1;0rad)
  Width = 2014
FEATURE [Part::Box] Box001001002001001001003002005003008  label="Vloerplank009"
  AttacherType = Attacher::AttachEngine3D
  Height = 15
  Length = 89
  Placement = pos=(904,347,250) rot=(0,0,1;0rad)
  Width = 2014
FEATURE [Part::Box] Box001001002001001001003002005003009  label="Vloerplank010"
  AttacherType = Attacher::AttachEngine3D
  Height = 15
  Length = 89
  Placement = pos=(993,347,250) rot=(0,0,1;0rad)
  Width = 2014
FEATURE [Part::Box] Box001001002001001001003002005003010  label="Vloerplank011"
  AttacherType = Attacher::AttachEngine3D
  Height = 15
  Length = 89
  Placement = pos=(1082,347,250) rot=(0,0,1;0rad)
  Width = 2014
FEATURE [Part::Box] Box001001002001001001003002005003011  label="Vloerplank012"
  AttacherType = Attacher::AttachEngine3D
  Height = 15
  Length = 89
  Placement = pos=(1171,347,250) rot=(0,0,1;0rad)
  Width = 2014
FEATURE [Part::Box] Box001001002001001001003002005003012  label="Vloerplank013"
  AttacherType = Attacher::AttachEngine3D
  Height = 15
  Length = 89
  Placement = pos=(1260,347,250) rot=(0,0,1;0rad)
  Width = 2014
FEATURE [Part::Box] Box001001002001001001003002005003013  label="Vloerplank014"
  AttacherType = Attacher::AttachEngine3D
  Height = 15
  Length = 89
  Placement = pos=(1349,347,250) rot=(0,0,1;0rad)
  Width = 2014
FEATURE [Part::Box] Box001001002001001001003002005003014  label="Vloerplank015"
  AttacherType = Attacher::AttachEngine3D
  Height = 15
  Length = 89
  Placement = pos=(1438,347,250) rot=(0,0,1;0rad)
  Width = 2014
FEATURE [Part::Box] Box001001002001001001003002005003015  label="Vloerplank016"
  AttacherType = Attacher::AttachEngine3D
  Height = 15
  Length = 89
  Placement = pos=(1527,347,250) rot=(0,0,1;0rad)
  Width = 2014
FEATURE [Part::Box] Box001001002001001001003002005003016  label="Vloerplank017"
  AttacherType = Attacher::AttachEngine3D
  Height = 15
  Length = 89
  Placement = pos=(1616,347,250) rot=(0,0,1;0rad)
  Width = 2014
FEATURE [Part::Box] Box001001002001001001003002005003017  label="Vloerplank018"
  AttacherType = Attacher::AttachEngine3D
  Height = 15
  Length = 89
  Placement = pos=(1705,347,250) rot=(0,0,1;0rad)
  Width = 2014
FEATURE [Part::Box] Box001001002001001001003002005003018  label="Vloerplank019"
  AttacherType = Attacher::AttachEngine3D
  Height = 15
  Length = 89
  Placement = pos=(1794,347,250) rot=(0,0,1;0rad)
  Width = 2014
FEATURE [Part::Box] Box001001002001001001003002005003019  label="Vloerplank020"
  AttacherType = Attacher::AttachEngine3D
  Height = 15
  Length = 89
  Placement = pos=(1883,347,250) rot=(0,0,1;0rad)
  Width = 2014
FEATURE [Part::Box] Box001001002001001001003002005003020  label="Vloerplank021"
  AttacherType = Attacher::AttachEngine3D
  Height = 15
  Length = 34
  Placement = pos=(158,347,250) rot=(0,0,1;0rad)
  Width = 2014
FEATURE [Part::Compound] Compound  label="floor skeleton"
  Links = -> [Box001001002001001001003002006,Box001001002001001001003002005001,Box001001002001001001003002004001,Box001001002001001001003002001001,Box001001002001001001003002003001,Box001001002001001001003001001,Box001001002001001001003002002001,Box001001002001001001003002005002]
FEATURE [Part::Compound] Compound001  label="floor finish internal"
  Links = -> [Box001001002001001001003002005003020,Box001001002001001001003002005003,Box001001002001001001003002005003001,Box001001002001001001003002005003002,Box001001002001001001003002005003003,Box001001002001001001003002005003004,Box001001002001001001003002005003005,Box001001002001001001003002005003006,Box001001002001001001003002005003007,Box001001002001001001003002005003008,+11 more]
FEATURE [Part::Compound] Compound003  label="rear finish internal"
  Links = -> [Box001001002001001001003002005003022001003004002001003001004002002001004002003005001001001001001001002001002001001004001001002002001005005002010015002005001001001001001001002005001014,Box001001002001001001003002005003022001003004002001003001004002002001004002003005001001001001001001002001002001001004001001002002001005005002010015002005001001001001001001002005001014001,+20 more]
FEATURE [Part::Compound] Compound004  label="rear wall skeleton"
  Links = -> [Box001001002001001001003002005003022,Box001001002001001001003002005003022001002,Box001001002001001001003002005003022001003,Box001001002001001001003002005003022001003001,Box001001002001001001003002005003022001003002,Box001001002001001001003002005003022001003003,Box001001002001001001003002005003022001003004,Box001001002001001001003002005003022001003004001,+3 more]
FEATURE [Part::Compound] Compound006  label="left wall skeleton"
  Links = -> [Box001001002001001001003002005003022001003004002001,Box001001002001001001003002005003022001003004002001003,Box001001002001001001003002005003022001003004002001003001,Box001001002001001001003002005003022001003001001002002,Box001001002001001001003002005003022001003001001001001,Box001001002001001001003002005003022001003001001002003,Box001001002001001001003002005003022001003001001002001001,+2 more]
FEATURE [Part::Compound] Compound007  label="left finish internal"
  Links = -> [Box001001002001001001003002005003022001003004002001003001004002002001004002003005001001001001001001002001002001001004001001002002001005005002010015002005001001001001001001002005001014020001001001022021,+21 more]
FEATURE [Part::Compound] Compound009  label="right finish internal"
  Links = -> [Box001001002001001001003002005003022001003004002001003001004002002001004002003005001001001001001001002001002001001004001001002002001005005002010015002005001001001001001001002005001014020001001001022021001,+21 more]
FEATURE [Part::Compound] Compound010  label="right wall skeleton"
  Links = -> [Box001001002001001001003002005003022001003004002001001,Box001001002001001001003002005003022001003004002001002,Box001001002001001001003002005003022001003001001,Box001001002001001001003002005003022001003001001001,Box001001002001001001003002005003022001003001001002,Box001001002001001001003002005003022001003001001002001,Box001001002001001001003002005003022001003004002001003002,+2 more]
FEATURE [Part::Compound] Compound012  label="front wall skeleton"
  Links = -> [Box001001002001001001003002005003022001003004002001003001004001,Box001001002001001001003002005003022001,Box001001002001001001003002005003022001001,Box001001002001001001003002005003022001003004002001003001002,Box001001002001001001003002005003022001003001001002001002,Box001001002001001001003002005003022001003002001,Box001001002001001001003002005003022001003003001,+5 more]
FEATURE [Part::Compound] Compound013  label="front finish internal"
  Links = -> [Box001001002001001001003002005003022001003004002001003001004002002001004002003005001001001001001001002001002001001004001001002002001005005002010015002005001001001001001001002005001014020001001,Box001001002001001001003002005003022001003004002001003001004002002001004002003005001001001001001001002001002001001004001001002002001005005002010015002005001001001001001001002005001014020001001001,+42 more]
FEATURE [Part::Compound] Compound014  label="ceiling finish internal"
  Links = -> [Box001001002001001001003002005003022001003004002001003001004002002001004002003005001001001001001001002001002001001004001001002002001005005002010015002005001001001001001001002005001014020001001001022021001022,+20 more]
FEATURE [Part::Compound] Compound015  label="ceiling skeleton"
  Links = -> [Box001001002001001001003002,Box001001002001001001003,Box001001002001001001003001,Box001001002001001001003002001,Box001001002001001001003002002,Box001001002001001001003002003,Box001001002001001001003002004,Box001001002001001001003002005]
FEATURE [Part::Compound] Compound016  label="left battens"
  Links = -> [Box001001002001001001003002005003022001003004002001003001004002002001004002003005001001001001001001002001002001001004001001002002001005005002010015002005001001001,Box001001002001001001003002005003022001003004002001003001004002002001004002003005001001001001001001002001002001001004001001002002001005005002010015002005,+2 more]
FEATURE [Part::Compound] Compound017  label="front battens"
  Links = -> [Box001001002001001001003002005003022001003004002001003001004002002001004002003005001001001001001001002001002001001004001001002002001005005002010015002005001001001001001001001,Box001001002001001001003002005003022001003004002001003001004002002001004002003005001001001001001001002001002001001004001001002002001005005002010015002005001001001001,+2 more]
FEATURE [Part::Compound] Compound018  label="right battens"
  Links = -> [Box001001002001001001003002005003022001003004002001003001004002002001004002003005001001001001001001002001002001001004001001002002001005005002010015002005001001001001001001006,Box001001002001001001003002005003022001003004002001003001004002002001004002003005001001001001001001002001002001001004001001002002001005005002010015002005001001001001001001003,+2 more]
FEATURE [Part::Compound] Compound019  label="rear battens"
  Links = -> [Box001001002001001001003002005003022001003004002001003001004002002001004002003005001001001001001001002001002001001004001001002002001005005002010015002005001001001001001001001001,Box001001002001001001003002005003022001003004002001003001004002002001004002003005001001001001001001002001002001001004001001002002001005005002010015002005001001001001001001002002,+2 more]
FEATURE [Part::Compound] Compound020  label="door finish internal"
  Links = -> [Box001001002001001001003002005003022001003004002001003001004002002001004002003005001001001001001001002001002001001004001001002002001005005002010015002005001001001001001001002005001014020001001001022021001022015006002014005001,+26 more]
FEATURE [Part::Compound] Compound021  label="door skeleton"
  Links = -> [Box009001002,Box006,Box007,Box009,Box010,Box007001,Box008001,Box008001001,Box009001,Box010001,Box009001001,Cut001]
FEATURE [Part::Compound] Compound022  label="top bench skeleton"
  Links = -> [Box001001002001001001003002005003022001003004002001003001004002,Box001001002001001001003002005003022001003004002001003001004002002,Box001001002001001001003002005003022001003004002001003001004002002001,Box001001002001001001003002005003022001003004002001003001004002002001004002002,Box001001002001001001003002005003022001003004002001003001004002002001004002003005003005001,+4 more]
FEATURE [Part::Compound] Compound023  label="top bench finish"
  Links = -> [Box001001002001001001003002005003022001003004002001003001004002002001004002003005003005001001002003001,Box001001002001001001003002005003022001003004002001003001004002001,Box001001002001001001003002005003022001003004002001003001004002002001004002003,Box001001002001001001003002005003022001003004002001003001004002002001004002003001,+6 more]
FEATURE [Part::Compound] Compound024  label="top bench 2 skeleton"
  Links = -> [Box001001002001001001003002005003022001003004002001003001004002002001004002003005001001001001001001002001002001001004001001002002001005005002010015002005001001001001001001002005001008,Box001001002001001001003002005003022001003004002001003001004002002001004002003005003005001001002,Box001001002001001001003002005003022001003004002001003001004002002001004002001,+3 more]
FEATURE [Part::Compound] Compound025  label="top bench 2 finish"
  Links = -> [Box001001002001001001003002005003022001003004002001003001004002002001004001002,Box001001002001001001003002005003022001003004002001003001004002002001004002003005003,Box001001002001001001003002005003022001003004002001003001004002002001004002003005003001,Box001001002001001001003002005003022001003004002001003001004002002001004002003005003002,+5 more]
FEATURE [Part::Compound] Compound026  label="lower bench skeleton"
  Links = -> [Box001001002001001001003002005003022001003004002001003001004002002001004002003005003005001001001,Box001001002001001001003002005003022001003004002001003001004002002001001,Box001001002001001001003002005003022001003004002001003001004002002001002,Box001001002001001001003002005003022001003004002001003001004002002001003,Box001001002001001001003002005003022001003004002001003001004002002001003001,+4 more]
FEATURE [Part::Compound] Compound027  label="lower bench finish"
  Links = -> [Box001001002001001001003002005003022001003004002001003001004002001001001,Box001001002001001001003002005003022001003004002001003001004002001001,Box001001002001001001003002005003022001003004002001003001004002002001004002003005001,Box001001002001001001003002005003022001003004002001003001004002002001004002003005002,Box001001002001001001003002005003022001003004002001003001004002002001004002003001001,+5 more]
FEATURE [Part::Compound] Compound028  label="Skeleton"
  Links = -> [Compound,Compound004,Compound006,Compound010,Compound012,Compound015,Box001001002001001001003002005003021,Box001001002001001001003002005003021001]
FEATURE [Part::Compound] Compound029  label="Internal finish"
  Links = -> [Compound001,Compound003,Compound007,Compound009,Compound013,Compound014]
FEATURE [Part::Compound] Compound030  label="MDF cover"
  Links = -> [Box001001002001001001003002005003022001003004002001003001004002002001004002003005001001001001001001002001002001001004001001002002001005005002010015002005001001001001001001002005001014020001001001022021001022015006002014005003002001001002001,+6 more]
FEATURE [Part::Compound] Compound031  label="Battens"
  Links = -> [Compound016,Compound018,Compound017,Compound019]
FEATURE [Part::Compound] Compound032  label="External finish"
  Links = -> [Cut002003,Box001001002001001001003002005003022001003004002001003001004002002001004002003005001001001001001001002001002001001004001001002002001005005002010015002005001001001001001001002005001014020001001001022021001022015006002014005003002001,+2 more]
FEATURE [Part::Compound] Compound033  label="Door"
  Links = -> [Cut002002,Cut002001,Compound020,Compound021,Box001001002001001001003002005003022001003004002001003001004002002001004002003005001001001001001001002001002001001004001001002002001005005002010015002005001001001001001001002005001014020001001001022021001022015006,Fusion002,Fusion001,Fusion]
FEATURE [Part::Compound] Compound034  label="Doorframe"
  Links = -> [Box001001002001001001003002005003022001003004002001003001004002002001004002003005001001001001001001002001002001001004001001002002001005005002010015002005001001001001001001002005001012,Cut,Box001001002001001001003002005003022001003004002001003001004002002001004002003005001001001001001001002001002001001004001001002002001005005002010015002005001001001001001001002005001011,Box002,Box004,Box005,Box011,+5 more]
FEATURE [Part::Compound] Compound035  label="Bench skeleton"
  Links = -> [Compound022,Compound024,Compound026]
FEATURE [Part::Compound] Compound036  label="Bench finish"
  Links = -> [Compound023,Compound025,Compound027]
FEATURE [Part::Compound] Compound037  label="Heater protection"
  Links = -> [Box001001002001001001003002005003022001003004002001003001004002002001004002003005001001001001,Box001001002001001001003002005003022001003004002001003001004002002001004002003005001001001001001,Box001001002001001001003002005003022001003004002001003001004002002001004002003005001001001001001001,Box001001002001001001003002005003022001003004002001003001004002002001004002003005001001001001001001001,+3 more]
FEATURE [Part::Compound] Compound038  label="Backrests"
  Links = -> [Box001001002001001001003002005003022001003004002001003001004002002001004002003005001001001001001001002001002,Box001001002001001001003002005003022001003004002001003001004002002001004001,Box001001002001001001003002005003022001003004002001003001004002002001004002003005001001001001001001002001002001,+19 more]
FEATURE [Part::Compound] Compound039  label="380Vheater"
  Links = -> [Part__Mirroring001,Torus001001003,Torus001001002,Cylinder005001001,Torus001001001,Cylinder004001]
FEATURE [Part::Compound] Compound040  label="230Vlight"
  Links = -> [Cylinder005001001001,Cylinder003001,Cylinder005001,Cylinder004,Part__Mirroring,Torus001002]
FEATURE [Part::Compound] Compound041  label="Electricity"
  Links = -> [Box001001002001001001003002005003022001003004002001003001004002002001004002003005003005001001002004,Cylinder005,Cylinder004002,Fusion003,Compound039,Compound040]
